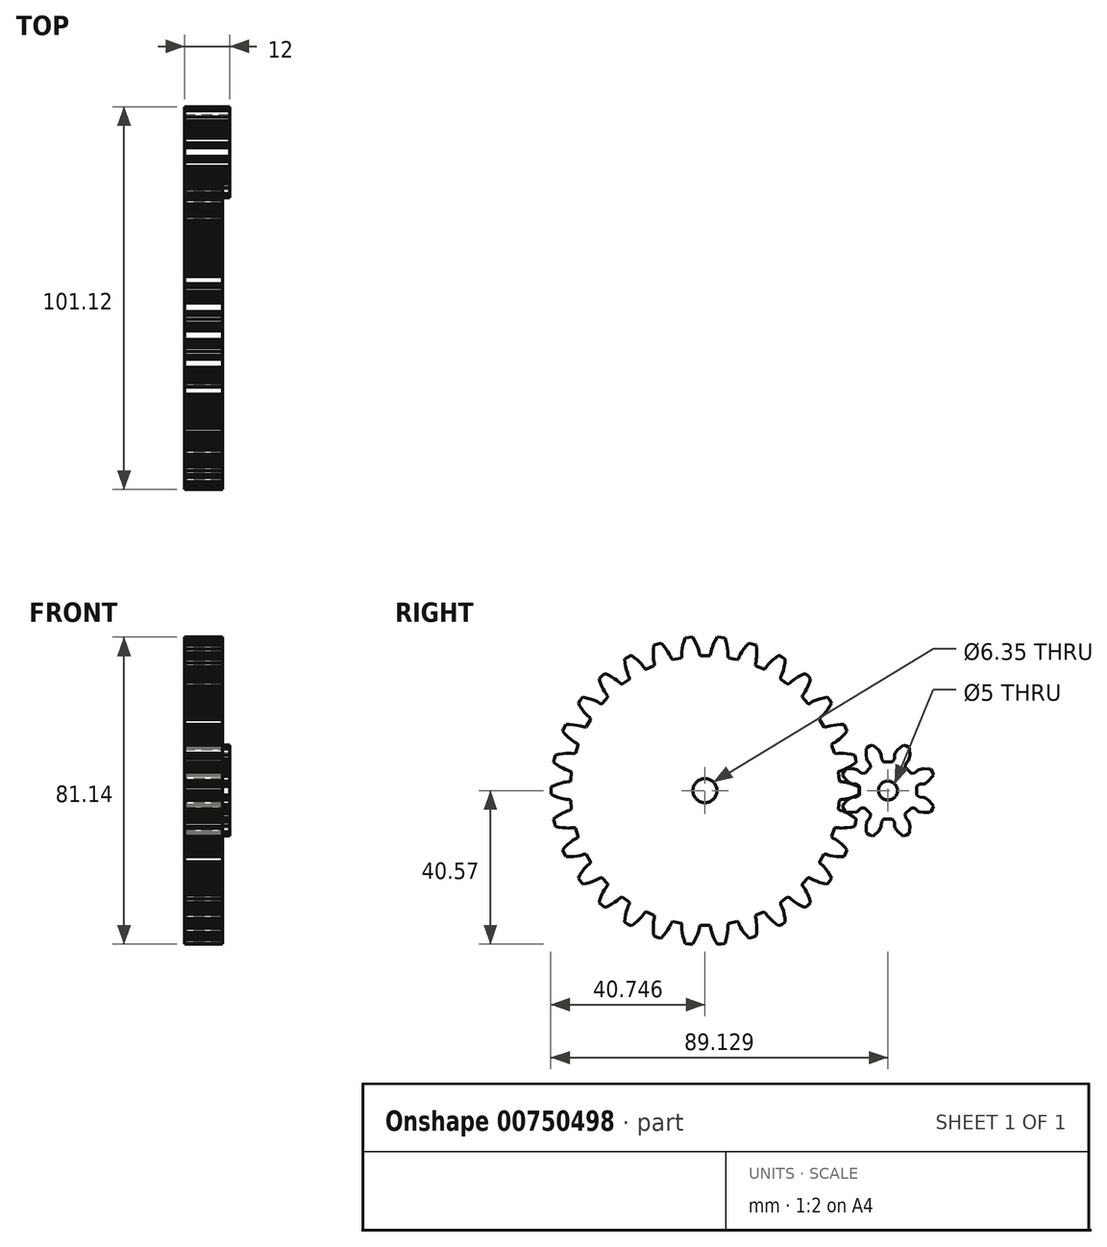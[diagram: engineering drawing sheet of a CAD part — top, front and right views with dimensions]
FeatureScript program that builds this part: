
annotation { "Feature Type Name" : "Feature", "Feature Type Description" : "" }
export const myFeature = defineFeature(function(context is Context, id is Id, definition is map)
    precondition{}
    {
        {
            var Q0;
            Q0=qCreatedBy(makeId("Right.planeOp"),FACE);
            var sketch = newSketch(context, id + "F0", { "sketchPlane" : qUnion([Q0])});
            skLineSegment(sketch, "E0", {"start": v(29.78, -9.42) * mm, "end": v(30.04, -8.47) * mm});
            skLineSegment(sketch, "E1", {"start": v(30.04, -8.47) * mm, "end": v(30.2, -7.5) * mm});
            skLineSegment(sketch, "E2", {"start": v(30.2, -7.5) * mm, "end": v(29.43, -6.92) * mm});
            skLineSegment(sketch, "E3", {"start": v(29.43, -6.92) * mm, "end": v(28.52, -6.34) * mm});
            skLineSegment(sketch, "E4", {"start": v(28.52, -6.34) * mm, "end": v(27.72, -5.9) * mm});
            skLineSegment(sketch, "E5", {"start": v(27.72, -5.9) * mm, "end": v(27.06, -5.6) * mm});
            skLineSegment(sketch, "E6", {"start": v(27.06, -5.6) * mm, "end": v(26.55, -5.4) * mm});
            skLineSegment(sketch, "E7", {"start": v(26.55, -5.4) * mm, "end": v(26, -5.23) * mm});
            skLineSegment(sketch, "E8", {"start": v(26, -5.23) * mm, "end": v(25.63, -5.05) * mm});
            skLineSegment(sketch, "E9", {"start": v(25.63, -5.05) * mm, "end": v(25.47, -4.85) * mm});
            skLineSegment(sketch, "E10", {"start": v(25.47, -4.85) * mm, "end": v(25.71, -2.59) * mm});
            skLineSegment(sketch, "E11", {"start": v(25.71, -2.59) * mm, "end": v(25.9, -2.43) * mm});
            skLineSegment(sketch, "E12", {"start": v(25.9, -2.43) * mm, "end": v(26.3, -2.33) * mm});
            skLineSegment(sketch, "E13", {"start": v(26.3, -2.33) * mm, "end": v(26.87, -2.28) * mm});
            skLineSegment(sketch, "E14", {"start": v(26.87, -2.28) * mm, "end": v(27.42, -2.2) * mm});
            skLineSegment(sketch, "E15", {"start": v(27.42, -2.2) * mm, "end": v(28.13, -2.04) * mm});
            skLineSegment(sketch, "E16", {"start": v(28.13, -2.04) * mm, "end": v(29, -1.77) * mm});
            skLineSegment(sketch, "E17", {"start": v(29, -1.77) * mm, "end": v(30, -1.39) * mm});
            skLineSegment(sketch, "E18", {"start": v(30, -1.39) * mm, "end": v(30.88, -0.98) * mm});
            skLineSegment(sketch, "E19", {"start": v(30.88, -0.98) * mm, "end": v(30.93, 0) * mm});
            skLineSegment(sketch, "E20", {"start": v(30.93, 0) * mm, "end": v(30.88, 0.98) * mm});
            skLineSegment(sketch, "E21", {"start": v(30.88, 0.98) * mm, "end": v(30, 1.39) * mm});
            skLineSegment(sketch, "E22", {"start": v(30, 1.39) * mm, "end": v(29, 1.77) * mm});
            skLineSegment(sketch, "E23", {"start": v(29, 1.77) * mm, "end": v(28.13, 2.04) * mm});
            skLineSegment(sketch, "E24", {"start": v(28.13, 2.04) * mm, "end": v(27.42, 2.2) * mm});
            skLineSegment(sketch, "E25", {"start": v(27.42, 2.2) * mm, "end": v(26.87, 2.28) * mm});
            skLineSegment(sketch, "E26", {"start": v(26.87, 2.28) * mm, "end": v(26.3, 2.33) * mm});
            skLineSegment(sketch, "E27", {"start": v(26.3, 2.33) * mm, "end": v(25.9, 2.43) * mm});
            skLineSegment(sketch, "E28", {"start": v(25.9, 2.43) * mm, "end": v(25.71, 2.59) * mm});
            skLineSegment(sketch, "E29", {"start": v(25.71, 2.59) * mm, "end": v(25.47, 4.85) * mm});
            skLineSegment(sketch, "E30", {"start": v(25.47, 4.85) * mm, "end": v(25.63, 5.05) * mm});
            skLineSegment(sketch, "E31", {"start": v(25.63, 5.05) * mm, "end": v(26, 5.23) * mm});
            skLineSegment(sketch, "E32", {"start": v(26, 5.23) * mm, "end": v(26.55, 5.4) * mm});
            skLineSegment(sketch, "E33", {"start": v(26.55, 5.4) * mm, "end": v(27.06, 5.6) * mm});
            skLineSegment(sketch, "E34", {"start": v(27.06, 5.6) * mm, "end": v(27.72, 5.9) * mm});
            skLineSegment(sketch, "E35", {"start": v(27.72, 5.9) * mm, "end": v(28.52, 6.34) * mm});
            skLineSegment(sketch, "E36", {"start": v(28.52, 6.34) * mm, "end": v(29.43, 6.92) * mm});
            skLineSegment(sketch, "E37", {"start": v(29.43, 6.92) * mm, "end": v(30.2, 7.5) * mm});
            skLineSegment(sketch, "E38", {"start": v(30.2, 7.5) * mm, "end": v(30.04, 8.47) * mm});
            skLineSegment(sketch, "E39", {"start": v(30.04, 8.47) * mm, "end": v(29.78, 9.42) * mm});
            skLineSegment(sketch, "E40", {"start": v(29.78, 9.42) * mm, "end": v(28.85, 9.64) * mm});
            skLineSegment(sketch, "E41", {"start": v(28.85, 9.64) * mm, "end": v(27.78, 9.8) * mm});
            skLineSegment(sketch, "E42", {"start": v(27.78, 9.8) * mm, "end": v(26.88, 9.88) * mm});
            skLineSegment(sketch, "E43", {"start": v(26.88, 9.88) * mm, "end": v(26.15, 9.9) * mm});
            skLineSegment(sketch, "E44", {"start": v(26.15, 9.9) * mm, "end": v(25.6, 9.86) * mm});
            skLineSegment(sketch, "E45", {"start": v(25.6, 9.86) * mm, "end": v(25.02, 9.79) * mm});
            skLineSegment(sketch, "E46", {"start": v(25.02, 9.79) * mm, "end": v(24.62, 9.8) * mm});
            skLineSegment(sketch, "E47", {"start": v(24.62, 9.8) * mm, "end": v(24.4, 9.92) * mm});
            skLineSegment(sketch, "E48", {"start": v(24.4, 9.92) * mm, "end": v(23.7, 12.08) * mm});
            skLineSegment(sketch, "E49", {"start": v(23.7, 12.08) * mm, "end": v(23.8, 12.3) * mm});
            skLineSegment(sketch, "E50", {"start": v(23.8, 12.3) * mm, "end": v(24.12, 12.56) * mm});
            skLineSegment(sketch, "E51", {"start": v(24.12, 12.56) * mm, "end": v(24.63, 12.84) * mm});
            skLineSegment(sketch, "E52", {"start": v(24.63, 12.84) * mm, "end": v(25.1, 13.14) * mm});
            skLineSegment(sketch, "E53", {"start": v(25.1, 13.14) * mm, "end": v(25.68, 13.57) * mm});
            skLineSegment(sketch, "E54", {"start": v(25.68, 13.57) * mm, "end": v(26.36, 14.17) * mm});
            skLineSegment(sketch, "E55", {"start": v(26.36, 14.17) * mm, "end": v(27.13, 14.93) * mm});
            skLineSegment(sketch, "E56", {"start": v(27.13, 14.93) * mm, "end": v(27.76, 15.65) * mm});
            skLineSegment(sketch, "E57", {"start": v(27.76, 15.65) * mm, "end": v(27.4, 16.57) * mm});
            skLineSegment(sketch, "E58", {"start": v(27.4, 16.57) * mm, "end": v(26.96, 17.45) * mm});
            skLineSegment(sketch, "E59", {"start": v(26.96, 17.45) * mm, "end": v(26, 17.46) * mm});
            skLineSegment(sketch, "E60", {"start": v(26, 17.46) * mm, "end": v(24.92, 17.4) * mm});
            skLineSegment(sketch, "E61", {"start": v(24.92, 17.4) * mm, "end": v(24.02, 17.3) * mm});
            skLineSegment(sketch, "E62", {"start": v(24.02, 17.3) * mm, "end": v(23.3, 17.15) * mm});
            skLineSegment(sketch, "E63", {"start": v(23.3, 17.15) * mm, "end": v(22.77, 17) * mm});
            skLineSegment(sketch, "E64", {"start": v(22.77, 17) * mm, "end": v(22.22, 16.82) * mm});
            skLineSegment(sketch, "E65", {"start": v(22.22, 16.82) * mm, "end": v(21.83, 16.75) * mm});
            skLineSegment(sketch, "E66", {"start": v(21.83, 16.75) * mm, "end": v(21.59, 16.81) * mm});
            skLineSegment(sketch, "E67", {"start": v(21.59, 16.81) * mm, "end": v(20.45, 18.79) * mm});
            skLineSegment(sketch, "E68", {"start": v(20.45, 18.79) * mm, "end": v(20.52, 19.03) * mm});
            skLineSegment(sketch, "E69", {"start": v(20.52, 19.03) * mm, "end": v(20.77, 19.34) * mm});
            skLineSegment(sketch, "E70", {"start": v(20.77, 19.34) * mm, "end": v(21.2, 19.72) * mm});
            skLineSegment(sketch, "E71", {"start": v(21.2, 19.72) * mm, "end": v(21.6, 20.1) * mm});
            skLineSegment(sketch, "E72", {"start": v(21.6, 20.1) * mm, "end": v(22.08, 20.66) * mm});
            skLineSegment(sketch, "E73", {"start": v(22.08, 20.66) * mm, "end": v(22.63, 21.38) * mm});
            skLineSegment(sketch, "E74", {"start": v(22.63, 21.38) * mm, "end": v(23.22, 22.28) * mm});
            skLineSegment(sketch, "E75", {"start": v(23.22, 22.28) * mm, "end": v(23.68, 23.12) * mm});
            skLineSegment(sketch, "E76", {"start": v(23.68, 23.12) * mm, "end": v(23.15, 23.95) * mm});
            skLineSegment(sketch, "E77", {"start": v(23.15, 23.95) * mm, "end": v(22.53, 24.71) * mm});
            skLineSegment(sketch, "E78", {"start": v(22.53, 24.71) * mm, "end": v(21.59, 24.53) * mm});
            skLineSegment(sketch, "E79", {"start": v(21.59, 24.53) * mm, "end": v(20.54, 24.25) * mm});
            skLineSegment(sketch, "E80", {"start": v(20.54, 24.25) * mm, "end": v(19.69, 23.95) * mm});
            skLineSegment(sketch, "E81", {"start": v(19.69, 23.95) * mm, "end": v(19.02, 23.66) * mm});
            skLineSegment(sketch, "E82", {"start": v(19.02, 23.66) * mm, "end": v(18.52, 23.41) * mm});
            skLineSegment(sketch, "E83", {"start": v(18.52, 23.41) * mm, "end": v(18.03, 23.11) * mm});
            skLineSegment(sketch, "E84", {"start": v(18.03, 23.11) * mm, "end": v(17.65, 22.97) * mm});
            skLineSegment(sketch, "E85", {"start": v(17.65, 22.97) * mm, "end": v(17.4, 22.98) * mm});
            skLineSegment(sketch, "E86", {"start": v(17.4, 22.98) * mm, "end": v(15.88, 24.67) * mm});
            skLineSegment(sketch, "E87", {"start": v(15.88, 24.67) * mm, "end": v(15.9, 24.92) * mm});
            skLineSegment(sketch, "E88", {"start": v(15.9, 24.92) * mm, "end": v(16.08, 25.27) * mm});
            skLineSegment(sketch, "E89", {"start": v(16.08, 25.27) * mm, "end": v(16.43, 25.74) * mm});
            skLineSegment(sketch, "E90", {"start": v(16.43, 25.74) * mm, "end": v(16.73, 26.2) * mm});
            skLineSegment(sketch, "E91", {"start": v(16.73, 26.2) * mm, "end": v(17.09, 26.84) * mm});
            skLineSegment(sketch, "E92", {"start": v(17.09, 26.84) * mm, "end": v(17.47, 27.66) * mm});
            skLineSegment(sketch, "E93", {"start": v(17.47, 27.66) * mm, "end": v(17.86, 28.67) * mm});
            skLineSegment(sketch, "E94", {"start": v(17.86, 28.67) * mm, "end": v(18.14, 29.58) * mm});
            skLineSegment(sketch, "E95", {"start": v(18.14, 29.58) * mm, "end": v(17.45, 30.28) * mm});
            skLineSegment(sketch, "E96", {"start": v(17.45, 30.28) * mm, "end": v(16.68, 30.9) * mm});
            skLineSegment(sketch, "E97", {"start": v(16.68, 30.9) * mm, "end": v(15.8, 30.52) * mm});
            skLineSegment(sketch, "E98", {"start": v(15.8, 30.52) * mm, "end": v(14.84, 30.03) * mm});
            skLineSegment(sketch, "E99", {"start": v(14.84, 30.03) * mm, "end": v(14.06, 29.56) * mm});
            skLineSegment(sketch, "E100", {"start": v(14.06, 29.56) * mm, "end": v(13.47, 29.14) * mm});
            skLineSegment(sketch, "E101", {"start": v(13.47, 29.14) * mm, "end": v(13.04, 28.8) * mm});
            skLineSegment(sketch, "E102", {"start": v(13.04, 28.8) * mm, "end": v(12.61, 28.4) * mm});
            skLineSegment(sketch, "E103", {"start": v(12.61, 28.4) * mm, "end": v(12.28, 28.17) * mm});
            skLineSegment(sketch, "E104", {"start": v(12.28, 28.17) * mm, "end": v(12.03, 28.13) * mm});
            skLineSegment(sketch, "E105", {"start": v(12.03, 28.13) * mm, "end": v(10.2, 29.47) * mm});
            skLineSegment(sketch, "E106", {"start": v(10.2, 29.47) * mm, "end": v(10.15, 29.72) * mm});
            skLineSegment(sketch, "E107", {"start": v(10.15, 29.72) * mm, "end": v(10.26, 30.1) * mm});
            skLineSegment(sketch, "E108", {"start": v(10.26, 30.1) * mm, "end": v(10.5, 30.63) * mm});
            skLineSegment(sketch, "E109", {"start": v(10.5, 30.63) * mm, "end": v(10.7, 31.15) * mm});
            skLineSegment(sketch, "E110", {"start": v(10.7, 31.15) * mm, "end": v(10.92, 31.84) * mm});
            skLineSegment(sketch, "E111", {"start": v(10.92, 31.84) * mm, "end": v(11.13, 32.73) * mm});
            skLineSegment(sketch, "E112", {"start": v(11.13, 32.73) * mm, "end": v(11.3, 33.8) * mm});
            skLineSegment(sketch, "E113", {"start": v(11.3, 33.8) * mm, "end": v(11.38, 34.75) * mm});
            skLineSegment(sketch, "E114", {"start": v(11.38, 34.75) * mm, "end": v(10.56, 35.29) * mm});
            skLineSegment(sketch, "E115", {"start": v(10.56, 35.29) * mm, "end": v(9.68, 35.73) * mm});
            skLineSegment(sketch, "E116", {"start": v(9.68, 35.73) * mm, "end": v(8.9, 35.18) * mm});
            skLineSegment(sketch, "E117", {"start": v(8.9, 35.18) * mm, "end": v(8.06, 34.5) * mm});
            skLineSegment(sketch, "E118", {"start": v(8.06, 34.5) * mm, "end": v(7.4, 33.88) * mm});
            skLineSegment(sketch, "E119", {"start": v(7.4, 33.88) * mm, "end": v(6.9, 33.34) * mm});
            skLineSegment(sketch, "E120", {"start": v(6.9, 33.34) * mm, "end": v(6.55, 32.91) * mm});
            skLineSegment(sketch, "E121", {"start": v(6.55, 32.91) * mm, "end": v(6.22, 32.44) * mm});
            skLineSegment(sketch, "E122", {"start": v(6.22, 32.44) * mm, "end": v(5.94, 32.15) * mm});
            skLineSegment(sketch, "E123", {"start": v(5.94, 32.15) * mm, "end": v(5.7, 32.06) * mm});
            skLineSegment(sketch, "E124", {"start": v(5.7, 32.06) * mm, "end": v(3.63, 32.99) * mm});
            skLineSegment(sketch, "E125", {"start": v(3.63, 32.99) * mm, "end": v(3.54, 33.22) * mm});
            skLineSegment(sketch, "E126", {"start": v(3.54, 33.22) * mm, "end": v(3.56, 33.62) * mm});
            skLineSegment(sketch, "E127", {"start": v(3.56, 33.62) * mm, "end": v(3.7, 34.19) * mm});
            skLineSegment(sketch, "E128", {"start": v(3.7, 34.19) * mm, "end": v(3.78, 34.73) * mm});
            skLineSegment(sketch, "E129", {"start": v(3.78, 34.73) * mm, "end": v(3.85, 35.46) * mm});
            skLineSegment(sketch, "E130", {"start": v(3.85, 35.46) * mm, "end": v(3.86, 36.36) * mm});
            skLineSegment(sketch, "E131", {"start": v(3.86, 36.36) * mm, "end": v(3.81, 37.44) * mm});
            skLineSegment(sketch, "E132", {"start": v(3.81, 37.44) * mm, "end": v(3.7, 38.4) * mm});
            skLineSegment(sketch, "E133", {"start": v(3.7, 38.4) * mm, "end": v(2.78, 38.75) * mm});
            skLineSegment(sketch, "E134", {"start": v(2.78, 38.75) * mm, "end": v(1.82, 39) * mm});
            skLineSegment(sketch, "E135", {"start": v(1.82, 39) * mm, "end": v(1.17, 38.3) * mm});
            skLineSegment(sketch, "E136", {"start": v(1.17, 38.3) * mm, "end": v(0.5, 37.46) * mm});
            skLineSegment(sketch, "E137", {"start": v(0.5, 37.46) * mm, "end": v(-0.02, 36.72) * mm});
            skLineSegment(sketch, "E138", {"start": v(-0.02, 36.72) * mm, "end": v(-0.4, 36.1) * mm});
            skLineSegment(sketch, "E139", {"start": v(-0.4, 36.1) * mm, "end": v(-0.65, 35.6) * mm});
            skLineSegment(sketch, "E140", {"start": v(-0.65, 35.6) * mm, "end": v(-0.87, 35.06) * mm});
            skLineSegment(sketch, "E141", {"start": v(-0.87, 35.06) * mm, "end": v(-1.1, 34.72) * mm});
            skLineSegment(sketch, "E142", {"start": v(-1.1, 34.72) * mm, "end": v(-1.3, 34.59) * mm});
            skLineSegment(sketch, "E143", {"start": v(-1.3, 34.59) * mm, "end": v(-3.53, 35.06) * mm});
            skLineSegment(sketch, "E144", {"start": v(-3.53, 35.06) * mm, "end": v(-3.66, 35.27) * mm});
            skLineSegment(sketch, "E145", {"start": v(-3.66, 35.27) * mm, "end": v(-3.72, 35.67) * mm});
            skLineSegment(sketch, "E146", {"start": v(-3.72, 35.67) * mm, "end": v(-3.7, 36.25) * mm});
            skLineSegment(sketch, "E147", {"start": v(-3.7, 36.25) * mm, "end": v(-3.74, 36.8) * mm});
            skLineSegment(sketch, "E148", {"start": v(-3.74, 36.8) * mm, "end": v(-3.82, 37.52) * mm});
            skLineSegment(sketch, "E149", {"start": v(-3.82, 37.52) * mm, "end": v(-4, 38.41) * mm});
            skLineSegment(sketch, "E150", {"start": v(-4, 38.41) * mm, "end": v(-4.27, 39.46) * mm});
            skLineSegment(sketch, "E151", {"start": v(-4.27, 39.46) * mm, "end": v(-4.58, 40.37) * mm});
            skLineSegment(sketch, "E152", {"start": v(-4.58, 40.37) * mm, "end": v(-5.56, 40.52) * mm});
            skLineSegment(sketch, "E153", {"start": v(-5.56, 40.52) * mm, "end": v(-6.54, 40.57) * mm});
            skLineSegment(sketch, "E154", {"start": v(-6.54, 40.57) * mm, "end": v(-7.03, 39.75) * mm});
            skLineSegment(sketch, "E155", {"start": v(-7.03, 39.75) * mm, "end": v(-7.52, 38.78) * mm});
            skLineSegment(sketch, "E156", {"start": v(-7.52, 38.78) * mm, "end": v(-7.87, 37.95) * mm});
            skLineSegment(sketch, "E157", {"start": v(-7.87, 37.95) * mm, "end": v(-8.1, 37.26) * mm});
            skLineSegment(sketch, "E158", {"start": v(-8.1, 37.26) * mm, "end": v(-8.25, 36.72) * mm});
            skLineSegment(sketch, "E159", {"start": v(-8.25, 36.72) * mm, "end": v(-8.36, 36.15) * mm});
            skLineSegment(sketch, "E160", {"start": v(-8.36, 36.15) * mm, "end": v(-8.5, 35.78) * mm});
            skLineSegment(sketch, "E161", {"start": v(-8.5, 35.78) * mm, "end": v(-8.68, 35.6) * mm});
            skLineSegment(sketch, "E162", {"start": v(-8.68, 35.6) * mm, "end": v(-10.95, 35.6) * mm});
            skLineSegment(sketch, "E163", {"start": v(-10.95, 35.6) * mm, "end": v(-11.13, 35.78) * mm});
            skLineSegment(sketch, "E164", {"start": v(-11.13, 35.78) * mm, "end": v(-11.27, 36.15) * mm});
            skLineSegment(sketch, "E165", {"start": v(-11.27, 36.15) * mm, "end": v(-11.38, 36.72) * mm});
            skLineSegment(sketch, "E166", {"start": v(-11.38, 36.72) * mm, "end": v(-11.52, 37.26) * mm});
            skLineSegment(sketch, "E167", {"start": v(-11.52, 37.26) * mm, "end": v(-11.76, 37.95) * mm});
            skLineSegment(sketch, "E168", {"start": v(-11.76, 37.95) * mm, "end": v(-12.1, 38.78) * mm});
            skLineSegment(sketch, "E169", {"start": v(-12.1, 38.78) * mm, "end": v(-12.6, 39.75) * mm});
            skLineSegment(sketch, "E170", {"start": v(-12.6, 39.75) * mm, "end": v(-13.09, 40.57) * mm});
            skLineSegment(sketch, "E171", {"start": v(-13.09, 40.57) * mm, "end": v(-14.07, 40.52) * mm});
            skLineSegment(sketch, "E172", {"start": v(-14.07, 40.52) * mm, "end": v(-15.05, 40.37) * mm});
            skLineSegment(sketch, "E173", {"start": v(-15.05, 40.37) * mm, "end": v(-15.36, 39.46) * mm});
            skLineSegment(sketch, "E174", {"start": v(-15.36, 39.46) * mm, "end": v(-15.63, 38.41) * mm});
            skLineSegment(sketch, "E175", {"start": v(-15.63, 38.41) * mm, "end": v(-15.8, 37.52) * mm});
            skLineSegment(sketch, "E176", {"start": v(-15.8, 37.52) * mm, "end": v(-15.9, 36.8) * mm});
            skLineSegment(sketch, "E177", {"start": v(-15.9, 36.8) * mm, "end": v(-15.92, 36.25) * mm});
            skLineSegment(sketch, "E178", {"start": v(-15.92, 36.25) * mm, "end": v(-15.9, 35.67) * mm});
            skLineSegment(sketch, "E179", {"start": v(-15.9, 35.67) * mm, "end": v(-15.97, 35.27) * mm});
            skLineSegment(sketch, "E180", {"start": v(-15.97, 35.27) * mm, "end": v(-16.1, 35.06) * mm});
            skLineSegment(sketch, "E181", {"start": v(-16.1, 35.06) * mm, "end": v(-18.33, 34.59) * mm});
            skLineSegment(sketch, "E182", {"start": v(-18.33, 34.59) * mm, "end": v(-18.54, 34.72) * mm});
            skLineSegment(sketch, "E183", {"start": v(-18.54, 34.72) * mm, "end": v(-18.75, 35.06) * mm});
            skLineSegment(sketch, "E184", {"start": v(-18.75, 35.06) * mm, "end": v(-18.98, 35.6) * mm});
            skLineSegment(sketch, "E185", {"start": v(-18.98, 35.6) * mm, "end": v(-19.23, 36.1) * mm});
            skLineSegment(sketch, "E186", {"start": v(-19.23, 36.1) * mm, "end": v(-19.6, 36.72) * mm});
            skLineSegment(sketch, "E187", {"start": v(-19.6, 36.72) * mm, "end": v(-20.12, 37.46) * mm});
            skLineSegment(sketch, "E188", {"start": v(-20.12, 37.46) * mm, "end": v(-20.8, 38.3) * mm});
            skLineSegment(sketch, "E189", {"start": v(-20.8, 38.3) * mm, "end": v(-21.45, 39) * mm});
            skLineSegment(sketch, "E190", {"start": v(-21.45, 39) * mm, "end": v(-22.4, 38.75) * mm});
            skLineSegment(sketch, "E191", {"start": v(-22.4, 38.75) * mm, "end": v(-23.32, 38.4) * mm});
            skLineSegment(sketch, "E192", {"start": v(-23.32, 38.4) * mm, "end": v(-23.44, 37.44) * mm});
            skLineSegment(sketch, "E193", {"start": v(-23.44, 37.44) * mm, "end": v(-23.5, 36.36) * mm});
            skLineSegment(sketch, "E194", {"start": v(-23.5, 36.36) * mm, "end": v(-23.48, 35.46) * mm});
            skLineSegment(sketch, "E195", {"start": v(-23.48, 35.46) * mm, "end": v(-23.41, 34.73) * mm});
            skLineSegment(sketch, "E196", {"start": v(-23.41, 34.73) * mm, "end": v(-23.32, 34.19) * mm});
            skLineSegment(sketch, "E197", {"start": v(-23.32, 34.19) * mm, "end": v(-23.2, 33.62) * mm});
            skLineSegment(sketch, "E198", {"start": v(-23.2, 33.62) * mm, "end": v(-23.17, 33.22) * mm});
            skLineSegment(sketch, "E199", {"start": v(-23.17, 33.22) * mm, "end": v(-23.25, 32.99) * mm});
            skLineSegment(sketch, "E200", {"start": v(-23.25, 32.99) * mm, "end": v(-25.33, 32.06) * mm});
            skLineSegment(sketch, "E201", {"start": v(-25.33, 32.06) * mm, "end": v(-25.57, 32.15) * mm});
            skLineSegment(sketch, "E202", {"start": v(-25.57, 32.15) * mm, "end": v(-25.85, 32.44) * mm});
            skLineSegment(sketch, "E203", {"start": v(-25.85, 32.44) * mm, "end": v(-26.18, 32.91) * mm});
            skLineSegment(sketch, "E204", {"start": v(-26.18, 32.91) * mm, "end": v(-26.53, 33.34) * mm});
            skLineSegment(sketch, "E205", {"start": v(-26.53, 33.34) * mm, "end": v(-27.02, 33.88) * mm});
            skLineSegment(sketch, "E206", {"start": v(-27.02, 33.88) * mm, "end": v(-27.68, 34.5) * mm});
            skLineSegment(sketch, "E207", {"start": v(-27.68, 34.5) * mm, "end": v(-28.52, 35.18) * mm});
            skLineSegment(sketch, "E208", {"start": v(-28.52, 35.18) * mm, "end": v(-29.3, 35.73) * mm});
            skLineSegment(sketch, "E209", {"start": v(-29.3, 35.73) * mm, "end": v(-30.19, 35.29) * mm});
            skLineSegment(sketch, "E210", {"start": v(-30.19, 35.29) * mm, "end": v(-31.01, 34.75) * mm});
            skLineSegment(sketch, "E211", {"start": v(-31.01, 34.75) * mm, "end": v(-30.93, 33.8) * mm});
            skLineSegment(sketch, "E212", {"start": v(-30.93, 33.8) * mm, "end": v(-30.76, 32.73) * mm});
            skLineSegment(sketch, "E213", {"start": v(-30.76, 32.73) * mm, "end": v(-30.55, 31.84) * mm});
            skLineSegment(sketch, "E214", {"start": v(-30.55, 31.84) * mm, "end": v(-30.33, 31.15) * mm});
            skLineSegment(sketch, "E215", {"start": v(-30.33, 31.15) * mm, "end": v(-30.14, 30.63) * mm});
            skLineSegment(sketch, "E216", {"start": v(-30.14, 30.63) * mm, "end": v(-29.89, 30.1) * mm});
            skLineSegment(sketch, "E217", {"start": v(-29.89, 30.1) * mm, "end": v(-29.78, 29.72) * mm});
            skLineSegment(sketch, "E218", {"start": v(-29.78, 29.72) * mm, "end": v(-29.82, 29.47) * mm});
            skLineSegment(sketch, "E219", {"start": v(-29.82, 29.47) * mm, "end": v(-31.66, 28.13) * mm});
            skLineSegment(sketch, "E220", {"start": v(-31.66, 28.13) * mm, "end": v(-31.9, 28.17) * mm});
            skLineSegment(sketch, "E221", {"start": v(-31.9, 28.17) * mm, "end": v(-32.24, 28.4) * mm});
            skLineSegment(sketch, "E222", {"start": v(-32.24, 28.4) * mm, "end": v(-32.67, 28.8) * mm});
            skLineSegment(sketch, "E223", {"start": v(-32.67, 28.8) * mm, "end": v(-33.1, 29.14) * mm});
            skLineSegment(sketch, "E224", {"start": v(-33.1, 29.14) * mm, "end": v(-33.7, 29.56) * mm});
            skLineSegment(sketch, "E225", {"start": v(-33.7, 29.56) * mm, "end": v(-34.47, 30.03) * mm});
            skLineSegment(sketch, "E226", {"start": v(-34.47, 30.03) * mm, "end": v(-35.43, 30.52) * mm});
            skLineSegment(sketch, "E227", {"start": v(-35.43, 30.52) * mm, "end": v(-36.31, 30.9) * mm});
            skLineSegment(sketch, "E228", {"start": v(-36.31, 30.9) * mm, "end": v(-37.08, 30.28) * mm});
            skLineSegment(sketch, "E229", {"start": v(-37.08, 30.28) * mm, "end": v(-37.77, 29.58) * mm});
            skLineSegment(sketch, "E230", {"start": v(-37.77, 29.58) * mm, "end": v(-37.5, 28.67) * mm});
            skLineSegment(sketch, "E231", {"start": v(-37.5, 28.67) * mm, "end": v(-37.1, 27.66) * mm});
            skLineSegment(sketch, "E232", {"start": v(-37.1, 27.66) * mm, "end": v(-36.72, 26.84) * mm});
            skLineSegment(sketch, "E233", {"start": v(-36.72, 26.84) * mm, "end": v(-36.36, 26.2) * mm});
            skLineSegment(sketch, "E234", {"start": v(-36.36, 26.2) * mm, "end": v(-36.06, 25.74) * mm});
            skLineSegment(sketch, "E235", {"start": v(-36.06, 25.74) * mm, "end": v(-35.7, 25.27) * mm});
            skLineSegment(sketch, "E236", {"start": v(-35.7, 25.27) * mm, "end": v(-35.53, 24.92) * mm});
            skLineSegment(sketch, "E237", {"start": v(-35.53, 24.92) * mm, "end": v(-35.5, 24.67) * mm});
            skLineSegment(sketch, "E238", {"start": v(-35.5, 24.67) * mm, "end": v(-37.03, 22.98) * mm});
            skLineSegment(sketch, "E239", {"start": v(-37.03, 22.98) * mm, "end": v(-37.28, 22.97) * mm});
            skLineSegment(sketch, "E240", {"start": v(-37.28, 22.97) * mm, "end": v(-37.66, 23.11) * mm});
            skLineSegment(sketch, "E241", {"start": v(-37.66, 23.11) * mm, "end": v(-38.15, 23.41) * mm});
            skLineSegment(sketch, "E242", {"start": v(-38.15, 23.41) * mm, "end": v(-38.64, 23.66) * mm});
            skLineSegment(sketch, "E243", {"start": v(-38.64, 23.66) * mm, "end": v(-39.32, 23.95) * mm});
            skLineSegment(sketch, "E244", {"start": v(-39.32, 23.95) * mm, "end": v(-40.17, 24.25) * mm});
            skLineSegment(sketch, "E245", {"start": v(-40.17, 24.25) * mm, "end": v(-41.22, 24.53) * mm});
            skLineSegment(sketch, "E246", {"start": v(-41.22, 24.53) * mm, "end": v(-42.16, 24.71) * mm});
            skLineSegment(sketch, "E247", {"start": v(-42.16, 24.71) * mm, "end": v(-42.78, 23.95) * mm});
            skLineSegment(sketch, "E248", {"start": v(-42.78, 23.95) * mm, "end": v(-43.31, 23.12) * mm});
            skLineSegment(sketch, "E249", {"start": v(-43.31, 23.12) * mm, "end": v(-42.85, 22.28) * mm});
            skLineSegment(sketch, "E250", {"start": v(-42.85, 22.28) * mm, "end": v(-42.26, 21.38) * mm});
            skLineSegment(sketch, "E251", {"start": v(-42.26, 21.38) * mm, "end": v(-41.7, 20.66) * mm});
            skLineSegment(sketch, "E252", {"start": v(-41.7, 20.66) * mm, "end": v(-41.23, 20.1) * mm});
            skLineSegment(sketch, "E253", {"start": v(-41.23, 20.1) * mm, "end": v(-40.84, 19.72) * mm});
            skLineSegment(sketch, "E254", {"start": v(-40.84, 19.72) * mm, "end": v(-40.4, 19.34) * mm});
            skLineSegment(sketch, "E255", {"start": v(-40.4, 19.34) * mm, "end": v(-40.14, 19.03) * mm});
            skLineSegment(sketch, "E256", {"start": v(-40.14, 19.03) * mm, "end": v(-40.08, 18.79) * mm});
            skLineSegment(sketch, "E257", {"start": v(-40.08, 18.79) * mm, "end": v(-41.21, 16.81) * mm});
            skLineSegment(sketch, "E258", {"start": v(-41.21, 16.81) * mm, "end": v(-41.46, 16.75) * mm});
            skLineSegment(sketch, "E259", {"start": v(-41.46, 16.75) * mm, "end": v(-41.85, 16.82) * mm});
            skLineSegment(sketch, "E260", {"start": v(-41.85, 16.82) * mm, "end": v(-42.4, 17) * mm});
            skLineSegment(sketch, "E261", {"start": v(-42.4, 17) * mm, "end": v(-42.93, 17.15) * mm});
            skLineSegment(sketch, "E262", {"start": v(-42.93, 17.15) * mm, "end": v(-43.65, 17.3) * mm});
            skLineSegment(sketch, "E263", {"start": v(-43.65, 17.3) * mm, "end": v(-44.55, 17.4) * mm});
            skLineSegment(sketch, "E264", {"start": v(-44.55, 17.4) * mm, "end": v(-45.63, 17.46) * mm});
            skLineSegment(sketch, "E265", {"start": v(-45.63, 17.46) * mm, "end": v(-46.59, 17.45) * mm});
            skLineSegment(sketch, "E266", {"start": v(-46.59, 17.45) * mm, "end": v(-47.04, 16.57) * mm});
            skLineSegment(sketch, "E267", {"start": v(-47.04, 16.57) * mm, "end": v(-47.39, 15.65) * mm});
            skLineSegment(sketch, "E268", {"start": v(-47.39, 15.65) * mm, "end": v(-46.76, 14.93) * mm});
            skLineSegment(sketch, "E269", {"start": v(-46.76, 14.93) * mm, "end": v(-46, 14.17) * mm});
            skLineSegment(sketch, "E270", {"start": v(-46, 14.17) * mm, "end": v(-45.3, 13.57) * mm});
            skLineSegment(sketch, "E271", {"start": v(-45.3, 13.57) * mm, "end": v(-44.72, 13.14) * mm});
            skLineSegment(sketch, "E272", {"start": v(-44.72, 13.14) * mm, "end": v(-44.26, 12.84) * mm});
            skLineSegment(sketch, "E273", {"start": v(-44.26, 12.84) * mm, "end": v(-43.75, 12.56) * mm});
            skLineSegment(sketch, "E274", {"start": v(-43.75, 12.56) * mm, "end": v(-43.44, 12.3) * mm});
            skLineSegment(sketch, "E275", {"start": v(-43.44, 12.3) * mm, "end": v(-43.32, 12.08) * mm});
            skLineSegment(sketch, "E276", {"start": v(-43.32, 12.08) * mm, "end": v(-44.02, 9.92) * mm});
            skLineSegment(sketch, "E277", {"start": v(-44.02, 9.92) * mm, "end": v(-44.25, 9.8) * mm});
            skLineSegment(sketch, "E278", {"start": v(-44.25, 9.8) * mm, "end": v(-44.65, 9.79) * mm});
            skLineSegment(sketch, "E279", {"start": v(-44.65, 9.79) * mm, "end": v(-45.22, 9.86) * mm});
            skLineSegment(sketch, "E280", {"start": v(-45.22, 9.86) * mm, "end": v(-45.78, 9.9) * mm});
            skLineSegment(sketch, "E281", {"start": v(-45.78, 9.9) * mm, "end": v(-46.5, 9.88) * mm});
            skLineSegment(sketch, "E282", {"start": v(-46.5, 9.88) * mm, "end": v(-47.4, 9.8) * mm});
            skLineSegment(sketch, "E283", {"start": v(-47.4, 9.8) * mm, "end": v(-48.48, 9.64) * mm});
            skLineSegment(sketch, "E284", {"start": v(-48.48, 9.64) * mm, "end": v(-49.41, 9.42) * mm});
            skLineSegment(sketch, "E285", {"start": v(-49.41, 9.42) * mm, "end": v(-49.67, 8.47) * mm});
            skLineSegment(sketch, "E286", {"start": v(-49.67, 8.47) * mm, "end": v(-49.82, 7.5) * mm});
            skLineSegment(sketch, "E287", {"start": v(-49.82, 7.5) * mm, "end": v(-49.05, 6.92) * mm});
            skLineSegment(sketch, "E288", {"start": v(-49.05, 6.92) * mm, "end": v(-48.15, 6.34) * mm});
            skLineSegment(sketch, "E289", {"start": v(-48.15, 6.34) * mm, "end": v(-47.35, 5.9) * mm});
            skLineSegment(sketch, "E290", {"start": v(-47.35, 5.9) * mm, "end": v(-46.7, 5.6) * mm});
            skLineSegment(sketch, "E291", {"start": v(-46.7, 5.6) * mm, "end": v(-46.17, 5.4) * mm});
            skLineSegment(sketch, "E292", {"start": v(-46.17, 5.4) * mm, "end": v(-45.62, 5.23) * mm});
            skLineSegment(sketch, "E293", {"start": v(-45.62, 5.23) * mm, "end": v(-45.26, 5.05) * mm});
            skLineSegment(sketch, "E294", {"start": v(-45.26, 5.05) * mm, "end": v(-45.1, 4.85) * mm});
            skLineSegment(sketch, "E295", {"start": v(-45.1, 4.85) * mm, "end": v(-45.34, 2.59) * mm});
            skLineSegment(sketch, "E296", {"start": v(-45.34, 2.59) * mm, "end": v(-45.54, 2.43) * mm});
            skLineSegment(sketch, "E297", {"start": v(-45.54, 2.43) * mm, "end": v(-45.92, 2.33) * mm});
            skLineSegment(sketch, "E298", {"start": v(-45.92, 2.33) * mm, "end": v(-46.5, 2.28) * mm});
            skLineSegment(sketch, "E299", {"start": v(-46.5, 2.28) * mm, "end": v(-47.05, 2.2) * mm});
            skLineSegment(sketch, "E300", {"start": v(-47.05, 2.2) * mm, "end": v(-47.76, 2.04) * mm});
            skLineSegment(sketch, "E301", {"start": v(-47.76, 2.04) * mm, "end": v(-48.63, 1.77) * mm});
            skLineSegment(sketch, "E302", {"start": v(-48.63, 1.77) * mm, "end": v(-49.64, 1.39) * mm});
            skLineSegment(sketch, "E303", {"start": v(-49.64, 1.39) * mm, "end": v(-50.5, 0.98) * mm});
            skLineSegment(sketch, "E304", {"start": v(-50.5, 0.98) * mm, "end": v(-50.56, 0) * mm});
            skLineSegment(sketch, "E305", {"start": v(-50.56, 0) * mm, "end": v(-50.5, -0.98) * mm});
            skLineSegment(sketch, "E306", {"start": v(-50.5, -0.98) * mm, "end": v(-49.64, -1.39) * mm});
            skLineSegment(sketch, "E307", {"start": v(-49.64, -1.39) * mm, "end": v(-48.63, -1.77) * mm});
            skLineSegment(sketch, "E308", {"start": v(-48.63, -1.77) * mm, "end": v(-47.76, -2.04) * mm});
            skLineSegment(sketch, "E309", {"start": v(-47.76, -2.04) * mm, "end": v(-47.05, -2.2) * mm});
            skLineSegment(sketch, "E310", {"start": v(-47.05, -2.2) * mm, "end": v(-46.5, -2.28) * mm});
            skLineSegment(sketch, "E311", {"start": v(-46.5, -2.28) * mm, "end": v(-45.92, -2.33) * mm});
            skLineSegment(sketch, "E312", {"start": v(-45.92, -2.33) * mm, "end": v(-45.54, -2.43) * mm});
            skLineSegment(sketch, "E313", {"start": v(-45.54, -2.43) * mm, "end": v(-45.34, -2.59) * mm});
            skLineSegment(sketch, "E314", {"start": v(-45.34, -2.59) * mm, "end": v(-45.1, -4.85) * mm});
            skLineSegment(sketch, "E315", {"start": v(-45.1, -4.85) * mm, "end": v(-45.26, -5.05) * mm});
            skLineSegment(sketch, "E316", {"start": v(-45.26, -5.05) * mm, "end": v(-45.62, -5.23) * mm});
            skLineSegment(sketch, "E317", {"start": v(-45.62, -5.23) * mm, "end": v(-46.17, -5.4) * mm});
            skLineSegment(sketch, "E318", {"start": v(-46.17, -5.4) * mm, "end": v(-46.7, -5.6) * mm});
            skLineSegment(sketch, "E319", {"start": v(-46.7, -5.6) * mm, "end": v(-47.35, -5.9) * mm});
            skLineSegment(sketch, "E320", {"start": v(-47.35, -5.9) * mm, "end": v(-48.15, -6.34) * mm});
            skLineSegment(sketch, "E321", {"start": v(-48.15, -6.34) * mm, "end": v(-49.05, -6.92) * mm});
            skLineSegment(sketch, "E322", {"start": v(-49.05, -6.92) * mm, "end": v(-49.82, -7.5) * mm});
            skLineSegment(sketch, "E323", {"start": v(-49.82, -7.5) * mm, "end": v(-49.67, -8.47) * mm});
            skLineSegment(sketch, "E324", {"start": v(-49.67, -8.47) * mm, "end": v(-49.41, -9.42) * mm});
            skLineSegment(sketch, "E325", {"start": v(-49.41, -9.42) * mm, "end": v(-48.48, -9.64) * mm});
            skLineSegment(sketch, "E326", {"start": v(-48.48, -9.64) * mm, "end": v(-47.4, -9.8) * mm});
            skLineSegment(sketch, "E327", {"start": v(-47.4, -9.8) * mm, "end": v(-46.5, -9.88) * mm});
            skLineSegment(sketch, "E328", {"start": v(-46.5, -9.88) * mm, "end": v(-45.78, -9.9) * mm});
            skLineSegment(sketch, "E329", {"start": v(-45.78, -9.9) * mm, "end": v(-45.22, -9.86) * mm});
            skLineSegment(sketch, "E330", {"start": v(-45.22, -9.86) * mm, "end": v(-44.65, -9.79) * mm});
            skLineSegment(sketch, "E331", {"start": v(-44.65, -9.79) * mm, "end": v(-44.25, -9.8) * mm});
            skLineSegment(sketch, "E332", {"start": v(-44.25, -9.8) * mm, "end": v(-44.02, -9.92) * mm});
            skLineSegment(sketch, "E333", {"start": v(-44.02, -9.92) * mm, "end": v(-43.32, -12.08) * mm});
            skLineSegment(sketch, "E334", {"start": v(-43.32, -12.08) * mm, "end": v(-43.44, -12.3) * mm});
            skLineSegment(sketch, "E335", {"start": v(-43.44, -12.3) * mm, "end": v(-43.75, -12.56) * mm});
            skLineSegment(sketch, "E336", {"start": v(-43.75, -12.56) * mm, "end": v(-44.26, -12.84) * mm});
            skLineSegment(sketch, "E337", {"start": v(-44.26, -12.84) * mm, "end": v(-44.72, -13.14) * mm});
            skLineSegment(sketch, "E338", {"start": v(-44.72, -13.14) * mm, "end": v(-45.3, -13.57) * mm});
            skLineSegment(sketch, "E339", {"start": v(-45.3, -13.57) * mm, "end": v(-46, -14.17) * mm});
            skLineSegment(sketch, "E340", {"start": v(-46, -14.17) * mm, "end": v(-46.76, -14.93) * mm});
            skLineSegment(sketch, "E341", {"start": v(-46.76, -14.93) * mm, "end": v(-47.39, -15.65) * mm});
            skLineSegment(sketch, "E342", {"start": v(-47.39, -15.65) * mm, "end": v(-47.04, -16.57) * mm});
            skLineSegment(sketch, "E343", {"start": v(-47.04, -16.57) * mm, "end": v(-46.59, -17.45) * mm});
            skLineSegment(sketch, "E344", {"start": v(-46.59, -17.45) * mm, "end": v(-45.63, -17.46) * mm});
            skLineSegment(sketch, "E345", {"start": v(-45.63, -17.46) * mm, "end": v(-44.55, -17.4) * mm});
            skLineSegment(sketch, "E346", {"start": v(-44.55, -17.4) * mm, "end": v(-43.65, -17.3) * mm});
            skLineSegment(sketch, "E347", {"start": v(-43.65, -17.3) * mm, "end": v(-42.93, -17.15) * mm});
            skLineSegment(sketch, "E348", {"start": v(-42.93, -17.15) * mm, "end": v(-42.4, -17) * mm});
            skLineSegment(sketch, "E349", {"start": v(-42.4, -17) * mm, "end": v(-41.85, -16.82) * mm});
            skLineSegment(sketch, "E350", {"start": v(-41.85, -16.82) * mm, "end": v(-41.46, -16.75) * mm});
            skLineSegment(sketch, "E351", {"start": v(-41.46, -16.75) * mm, "end": v(-41.21, -16.81) * mm});
            skLineSegment(sketch, "E352", {"start": v(-41.21, -16.81) * mm, "end": v(-40.08, -18.79) * mm});
            skLineSegment(sketch, "E353", {"start": v(-40.08, -18.79) * mm, "end": v(-40.14, -19.03) * mm});
            skLineSegment(sketch, "E354", {"start": v(-40.14, -19.03) * mm, "end": v(-40.4, -19.34) * mm});
            skLineSegment(sketch, "E355", {"start": v(-40.4, -19.34) * mm, "end": v(-40.84, -19.72) * mm});
            skLineSegment(sketch, "E356", {"start": v(-40.84, -19.72) * mm, "end": v(-41.23, -20.1) * mm});
            skLineSegment(sketch, "E357", {"start": v(-41.23, -20.1) * mm, "end": v(-41.7, -20.66) * mm});
            skLineSegment(sketch, "E358", {"start": v(-41.7, -20.66) * mm, "end": v(-42.26, -21.38) * mm});
            skLineSegment(sketch, "E359", {"start": v(-42.26, -21.38) * mm, "end": v(-42.85, -22.28) * mm});
            skLineSegment(sketch, "E360", {"start": v(-42.85, -22.28) * mm, "end": v(-43.31, -23.12) * mm});
            skLineSegment(sketch, "E361", {"start": v(-43.31, -23.12) * mm, "end": v(-42.78, -23.95) * mm});
            skLineSegment(sketch, "E362", {"start": v(-42.78, -23.95) * mm, "end": v(-42.16, -24.71) * mm});
            skLineSegment(sketch, "E363", {"start": v(-42.16, -24.71) * mm, "end": v(-41.22, -24.53) * mm});
            skLineSegment(sketch, "E364", {"start": v(-41.22, -24.53) * mm, "end": v(-40.17, -24.25) * mm});
            skLineSegment(sketch, "E365", {"start": v(-40.17, -24.25) * mm, "end": v(-39.32, -23.95) * mm});
            skLineSegment(sketch, "E366", {"start": v(-39.32, -23.95) * mm, "end": v(-38.64, -23.66) * mm});
            skLineSegment(sketch, "E367", {"start": v(-38.64, -23.66) * mm, "end": v(-38.15, -23.41) * mm});
            skLineSegment(sketch, "E368", {"start": v(-38.15, -23.41) * mm, "end": v(-37.66, -23.11) * mm});
            skLineSegment(sketch, "E369", {"start": v(-37.66, -23.11) * mm, "end": v(-37.28, -22.97) * mm});
            skLineSegment(sketch, "E370", {"start": v(-37.28, -22.97) * mm, "end": v(-37.03, -22.98) * mm});
            skLineSegment(sketch, "E371", {"start": v(-37.03, -22.98) * mm, "end": v(-35.5, -24.67) * mm});
            skLineSegment(sketch, "E372", {"start": v(-35.5, -24.67) * mm, "end": v(-35.53, -24.92) * mm});
            skLineSegment(sketch, "E373", {"start": v(-35.53, -24.92) * mm, "end": v(-35.7, -25.27) * mm});
            skLineSegment(sketch, "E374", {"start": v(-35.7, -25.27) * mm, "end": v(-36.06, -25.74) * mm});
            skLineSegment(sketch, "E375", {"start": v(-36.06, -25.74) * mm, "end": v(-36.36, -26.2) * mm});
            skLineSegment(sketch, "E376", {"start": v(-36.36, -26.2) * mm, "end": v(-36.72, -26.84) * mm});
            skLineSegment(sketch, "E377", {"start": v(-36.72, -26.84) * mm, "end": v(-37.1, -27.66) * mm});
            skLineSegment(sketch, "E378", {"start": v(-37.1, -27.66) * mm, "end": v(-37.5, -28.67) * mm});
            skLineSegment(sketch, "E379", {"start": v(-37.5, -28.67) * mm, "end": v(-37.77, -29.58) * mm});
            skLineSegment(sketch, "E380", {"start": v(-37.77, -29.58) * mm, "end": v(-37.08, -30.28) * mm});
            skLineSegment(sketch, "E381", {"start": v(-37.08, -30.28) * mm, "end": v(-36.31, -30.9) * mm});
            skLineSegment(sketch, "E382", {"start": v(-36.31, -30.9) * mm, "end": v(-35.43, -30.52) * mm});
            skLineSegment(sketch, "E383", {"start": v(-35.43, -30.52) * mm, "end": v(-34.47, -30.03) * mm});
            skLineSegment(sketch, "E384", {"start": v(-34.47, -30.03) * mm, "end": v(-33.7, -29.56) * mm});
            skLineSegment(sketch, "E385", {"start": v(-33.7, -29.56) * mm, "end": v(-33.1, -29.14) * mm});
            skLineSegment(sketch, "E386", {"start": v(-33.1, -29.14) * mm, "end": v(-32.67, -28.8) * mm});
            skLineSegment(sketch, "E387", {"start": v(-32.67, -28.8) * mm, "end": v(-32.24, -28.4) * mm});
            skLineSegment(sketch, "E388", {"start": v(-32.24, -28.4) * mm, "end": v(-31.9, -28.17) * mm});
            skLineSegment(sketch, "E389", {"start": v(-31.9, -28.17) * mm, "end": v(-31.66, -28.13) * mm});
            skLineSegment(sketch, "E390", {"start": v(-31.66, -28.13) * mm, "end": v(-29.82, -29.47) * mm});
            skLineSegment(sketch, "E391", {"start": v(-29.82, -29.47) * mm, "end": v(-29.78, -29.72) * mm});
            skLineSegment(sketch, "E392", {"start": v(-29.78, -29.72) * mm, "end": v(-29.89, -30.1) * mm});
            skLineSegment(sketch, "E393", {"start": v(-29.89, -30.1) * mm, "end": v(-30.14, -30.63) * mm});
            skLineSegment(sketch, "E394", {"start": v(-30.14, -30.63) * mm, "end": v(-30.33, -31.15) * mm});
            skLineSegment(sketch, "E395", {"start": v(-30.33, -31.15) * mm, "end": v(-30.55, -31.84) * mm});
            skLineSegment(sketch, "E396", {"start": v(-30.55, -31.84) * mm, "end": v(-30.76, -32.73) * mm});
            skLineSegment(sketch, "E397", {"start": v(-30.76, -32.73) * mm, "end": v(-30.93, -33.8) * mm});
            skLineSegment(sketch, "E398", {"start": v(-30.93, -33.8) * mm, "end": v(-31.01, -34.75) * mm});
            skLineSegment(sketch, "E399", {"start": v(-31.01, -34.75) * mm, "end": v(-30.19, -35.29) * mm});
            skLineSegment(sketch, "E400", {"start": v(-30.19, -35.29) * mm, "end": v(-29.3, -35.73) * mm});
            skLineSegment(sketch, "E401", {"start": v(-29.3, -35.73) * mm, "end": v(-28.52, -35.18) * mm});
            skLineSegment(sketch, "E402", {"start": v(-28.52, -35.18) * mm, "end": v(-27.68, -34.5) * mm});
            skLineSegment(sketch, "E403", {"start": v(-27.68, -34.5) * mm, "end": v(-27.02, -33.88) * mm});
            skLineSegment(sketch, "E404", {"start": v(-27.02, -33.88) * mm, "end": v(-26.53, -33.34) * mm});
            skLineSegment(sketch, "E405", {"start": v(-26.53, -33.34) * mm, "end": v(-26.18, -32.91) * mm});
            skLineSegment(sketch, "E406", {"start": v(-26.18, -32.91) * mm, "end": v(-25.85, -32.44) * mm});
            skLineSegment(sketch, "E407", {"start": v(-25.85, -32.44) * mm, "end": v(-25.57, -32.15) * mm});
            skLineSegment(sketch, "E408", {"start": v(-25.57, -32.15) * mm, "end": v(-25.33, -32.06) * mm});
            skLineSegment(sketch, "E409", {"start": v(-25.33, -32.06) * mm, "end": v(-23.25, -32.99) * mm});
            skLineSegment(sketch, "E410", {"start": v(-23.25, -32.99) * mm, "end": v(-23.17, -33.22) * mm});
            skLineSegment(sketch, "E411", {"start": v(-23.17, -33.22) * mm, "end": v(-23.2, -33.62) * mm});
            skLineSegment(sketch, "E412", {"start": v(-23.2, -33.62) * mm, "end": v(-23.32, -34.19) * mm});
            skLineSegment(sketch, "E413", {"start": v(-23.32, -34.19) * mm, "end": v(-23.41, -34.73) * mm});
            skLineSegment(sketch, "E414", {"start": v(-23.41, -34.73) * mm, "end": v(-23.48, -35.46) * mm});
            skLineSegment(sketch, "E415", {"start": v(-23.48, -35.46) * mm, "end": v(-23.5, -36.36) * mm});
            skLineSegment(sketch, "E416", {"start": v(-23.5, -36.36) * mm, "end": v(-23.44, -37.44) * mm});
            skLineSegment(sketch, "E417", {"start": v(-23.44, -37.44) * mm, "end": v(-23.32, -38.4) * mm});
            skLineSegment(sketch, "E418", {"start": v(-23.32, -38.4) * mm, "end": v(-22.4, -38.75) * mm});
            skLineSegment(sketch, "E419", {"start": v(-22.4, -38.75) * mm, "end": v(-21.45, -39) * mm});
            skLineSegment(sketch, "E420", {"start": v(-21.45, -39) * mm, "end": v(-20.8, -38.3) * mm});
            skLineSegment(sketch, "E421", {"start": v(-20.8, -38.3) * mm, "end": v(-20.12, -37.46) * mm});
            skLineSegment(sketch, "E422", {"start": v(-20.12, -37.46) * mm, "end": v(-19.6, -36.72) * mm});
            skLineSegment(sketch, "E423", {"start": v(-19.6, -36.72) * mm, "end": v(-19.23, -36.1) * mm});
            skLineSegment(sketch, "E424", {"start": v(-19.23, -36.1) * mm, "end": v(-18.98, -35.6) * mm});
            skLineSegment(sketch, "E425", {"start": v(-18.98, -35.6) * mm, "end": v(-18.75, -35.06) * mm});
            skLineSegment(sketch, "E426", {"start": v(-18.75, -35.06) * mm, "end": v(-18.54, -34.72) * mm});
            skLineSegment(sketch, "E427", {"start": v(-18.54, -34.72) * mm, "end": v(-18.33, -34.59) * mm});
            skLineSegment(sketch, "E428", {"start": v(-18.33, -34.59) * mm, "end": v(-16.1, -35.06) * mm});
            skLineSegment(sketch, "E429", {"start": v(-16.1, -35.06) * mm, "end": v(-15.97, -35.27) * mm});
            skLineSegment(sketch, "E430", {"start": v(-15.97, -35.27) * mm, "end": v(-15.9, -35.67) * mm});
            skLineSegment(sketch, "E431", {"start": v(-15.9, -35.67) * mm, "end": v(-15.92, -36.25) * mm});
            skLineSegment(sketch, "E432", {"start": v(-15.92, -36.25) * mm, "end": v(-15.9, -36.8) * mm});
            skLineSegment(sketch, "E433", {"start": v(-15.9, -36.8) * mm, "end": v(-15.8, -37.52) * mm});
            skLineSegment(sketch, "E434", {"start": v(-15.8, -37.52) * mm, "end": v(-15.63, -38.41) * mm});
            skLineSegment(sketch, "E435", {"start": v(-15.63, -38.41) * mm, "end": v(-15.36, -39.46) * mm});
            skLineSegment(sketch, "E436", {"start": v(-15.36, -39.46) * mm, "end": v(-15.05, -40.37) * mm});
            skLineSegment(sketch, "E437", {"start": v(-15.05, -40.37) * mm, "end": v(-14.07, -40.52) * mm});
            skLineSegment(sketch, "E438", {"start": v(-14.07, -40.52) * mm, "end": v(-13.09, -40.57) * mm});
            skLineSegment(sketch, "E439", {"start": v(-13.09, -40.57) * mm, "end": v(-12.6, -39.75) * mm});
            skLineSegment(sketch, "E440", {"start": v(-12.6, -39.75) * mm, "end": v(-12.1, -38.78) * mm});
            skLineSegment(sketch, "E441", {"start": v(-12.1, -38.78) * mm, "end": v(-11.76, -37.95) * mm});
            skLineSegment(sketch, "E442", {"start": v(-11.76, -37.95) * mm, "end": v(-11.52, -37.26) * mm});
            skLineSegment(sketch, "E443", {"start": v(-11.52, -37.26) * mm, "end": v(-11.38, -36.72) * mm});
            skLineSegment(sketch, "E444", {"start": v(-11.38, -36.72) * mm, "end": v(-11.27, -36.15) * mm});
            skLineSegment(sketch, "E445", {"start": v(-11.27, -36.15) * mm, "end": v(-11.13, -35.78) * mm});
            skLineSegment(sketch, "E446", {"start": v(-11.13, -35.78) * mm, "end": v(-10.95, -35.6) * mm});
            skLineSegment(sketch, "E447", {"start": v(-10.95, -35.6) * mm, "end": v(-8.68, -35.6) * mm});
            skLineSegment(sketch, "E448", {"start": v(-8.68, -35.6) * mm, "end": v(-8.5, -35.78) * mm});
            skLineSegment(sketch, "E449", {"start": v(-8.5, -35.78) * mm, "end": v(-8.36, -36.15) * mm});
            skLineSegment(sketch, "E450", {"start": v(-8.36, -36.15) * mm, "end": v(-8.25, -36.72) * mm});
            skLineSegment(sketch, "E451", {"start": v(-8.25, -36.72) * mm, "end": v(-8.1, -37.26) * mm});
            skLineSegment(sketch, "E452", {"start": v(-8.1, -37.26) * mm, "end": v(-7.87, -37.95) * mm});
            skLineSegment(sketch, "E453", {"start": v(-7.87, -37.95) * mm, "end": v(-7.52, -38.78) * mm});
            skLineSegment(sketch, "E454", {"start": v(-7.52, -38.78) * mm, "end": v(-7.03, -39.75) * mm});
            skLineSegment(sketch, "E455", {"start": v(-7.03, -39.75) * mm, "end": v(-6.54, -40.57) * mm});
            skLineSegment(sketch, "E456", {"start": v(-6.54, -40.57) * mm, "end": v(-5.56, -40.52) * mm});
            skLineSegment(sketch, "E457", {"start": v(-5.56, -40.52) * mm, "end": v(-4.58, -40.37) * mm});
            skLineSegment(sketch, "E458", {"start": v(-4.58, -40.37) * mm, "end": v(-4.27, -39.46) * mm});
            skLineSegment(sketch, "E459", {"start": v(-4.27, -39.46) * mm, "end": v(-4, -38.41) * mm});
            skLineSegment(sketch, "E460", {"start": v(-4, -38.41) * mm, "end": v(-3.82, -37.52) * mm});
            skLineSegment(sketch, "E461", {"start": v(-3.82, -37.52) * mm, "end": v(-3.74, -36.8) * mm});
            skLineSegment(sketch, "E462", {"start": v(-3.74, -36.8) * mm, "end": v(-3.7, -36.25) * mm});
            skLineSegment(sketch, "E463", {"start": v(-3.7, -36.25) * mm, "end": v(-3.72, -35.67) * mm});
            skLineSegment(sketch, "E464", {"start": v(-3.72, -35.67) * mm, "end": v(-3.66, -35.27) * mm});
            skLineSegment(sketch, "E465", {"start": v(-3.66, -35.27) * mm, "end": v(-3.53, -35.06) * mm});
            skLineSegment(sketch, "E466", {"start": v(-3.53, -35.06) * mm, "end": v(-1.3, -34.59) * mm});
            skLineSegment(sketch, "E467", {"start": v(-1.3, -34.59) * mm, "end": v(-1.1, -34.72) * mm});
            skLineSegment(sketch, "E468", {"start": v(-1.1, -34.72) * mm, "end": v(-0.87, -35.06) * mm});
            skLineSegment(sketch, "E469", {"start": v(-0.87, -35.06) * mm, "end": v(-0.65, -35.6) * mm});
            skLineSegment(sketch, "E470", {"start": v(-0.65, -35.6) * mm, "end": v(-0.4, -36.1) * mm});
            skLineSegment(sketch, "E471", {"start": v(-0.4, -36.1) * mm, "end": v(-0.02, -36.72) * mm});
            skLineSegment(sketch, "E472", {"start": v(-0.02, -36.72) * mm, "end": v(0.5, -37.46) * mm});
            skLineSegment(sketch, "E473", {"start": v(0.5, -37.46) * mm, "end": v(1.17, -38.3) * mm});
            skLineSegment(sketch, "E474", {"start": v(1.17, -38.3) * mm, "end": v(1.82, -39) * mm});
            skLineSegment(sketch, "E475", {"start": v(1.82, -39) * mm, "end": v(2.78, -38.75) * mm});
            skLineSegment(sketch, "E476", {"start": v(2.78, -38.75) * mm, "end": v(3.7, -38.4) * mm});
            skLineSegment(sketch, "E477", {"start": v(3.7, -38.4) * mm, "end": v(3.81, -37.44) * mm});
            skLineSegment(sketch, "E478", {"start": v(3.81, -37.44) * mm, "end": v(3.86, -36.36) * mm});
            skLineSegment(sketch, "E479", {"start": v(3.86, -36.36) * mm, "end": v(3.85, -35.46) * mm});
            skLineSegment(sketch, "E480", {"start": v(3.85, -35.46) * mm, "end": v(3.78, -34.73) * mm});
            skLineSegment(sketch, "E481", {"start": v(3.78, -34.73) * mm, "end": v(3.7, -34.19) * mm});
            skLineSegment(sketch, "E482", {"start": v(3.7, -34.19) * mm, "end": v(3.56, -33.62) * mm});
            skLineSegment(sketch, "E483", {"start": v(3.56, -33.62) * mm, "end": v(3.54, -33.22) * mm});
            skLineSegment(sketch, "E484", {"start": v(3.54, -33.22) * mm, "end": v(3.63, -32.99) * mm});
            skLineSegment(sketch, "E485", {"start": v(3.63, -32.99) * mm, "end": v(5.7, -32.06) * mm});
            skLineSegment(sketch, "E486", {"start": v(5.7, -32.06) * mm, "end": v(5.94, -32.15) * mm});
            skLineSegment(sketch, "E487", {"start": v(5.94, -32.15) * mm, "end": v(6.22, -32.44) * mm});
            skLineSegment(sketch, "E488", {"start": v(6.22, -32.44) * mm, "end": v(6.55, -32.91) * mm});
            skLineSegment(sketch, "E489", {"start": v(6.55, -32.91) * mm, "end": v(6.9, -33.34) * mm});
            skLineSegment(sketch, "E490", {"start": v(6.9, -33.34) * mm, "end": v(7.4, -33.88) * mm});
            skLineSegment(sketch, "E491", {"start": v(7.4, -33.88) * mm, "end": v(8.06, -34.5) * mm});
            skLineSegment(sketch, "E492", {"start": v(8.06, -34.5) * mm, "end": v(8.9, -35.18) * mm});
            skLineSegment(sketch, "E493", {"start": v(8.9, -35.18) * mm, "end": v(9.68, -35.73) * mm});
            skLineSegment(sketch, "E494", {"start": v(9.68, -35.73) * mm, "end": v(10.56, -35.29) * mm});
            skLineSegment(sketch, "E495", {"start": v(10.56, -35.29) * mm, "end": v(11.38, -34.75) * mm});
            skLineSegment(sketch, "E496", {"start": v(11.38, -34.75) * mm, "end": v(11.3, -33.8) * mm});
            skLineSegment(sketch, "E497", {"start": v(11.3, -33.8) * mm, "end": v(11.13, -32.73) * mm});
            skLineSegment(sketch, "E498", {"start": v(11.13, -32.73) * mm, "end": v(10.92, -31.84) * mm});
            skLineSegment(sketch, "E499", {"start": v(10.92, -31.84) * mm, "end": v(10.7, -31.15) * mm});
            skLineSegment(sketch, "E500", {"start": v(10.7, -31.15) * mm, "end": v(10.5, -30.63) * mm});
            skLineSegment(sketch, "E501", {"start": v(10.5, -30.63) * mm, "end": v(10.26, -30.1) * mm});
            skLineSegment(sketch, "E502", {"start": v(10.26, -30.1) * mm, "end": v(10.15, -29.72) * mm});
            skLineSegment(sketch, "E503", {"start": v(10.15, -29.72) * mm, "end": v(10.2, -29.47) * mm});
            skLineSegment(sketch, "E504", {"start": v(10.2, -29.47) * mm, "end": v(12.03, -28.13) * mm});
            skLineSegment(sketch, "E505", {"start": v(12.03, -28.13) * mm, "end": v(12.28, -28.17) * mm});
            skLineSegment(sketch, "E506", {"start": v(12.28, -28.17) * mm, "end": v(12.61, -28.4) * mm});
            skLineSegment(sketch, "E507", {"start": v(12.61, -28.4) * mm, "end": v(13.04, -28.8) * mm});
            skLineSegment(sketch, "E508", {"start": v(13.04, -28.8) * mm, "end": v(13.47, -29.14) * mm});
            skLineSegment(sketch, "E509", {"start": v(13.47, -29.14) * mm, "end": v(14.06, -29.56) * mm});
            skLineSegment(sketch, "E510", {"start": v(14.06, -29.56) * mm, "end": v(14.84, -30.03) * mm});
            skLineSegment(sketch, "E511", {"start": v(14.84, -30.03) * mm, "end": v(15.8, -30.52) * mm});
            skLineSegment(sketch, "E512", {"start": v(15.8, -30.52) * mm, "end": v(16.68, -30.9) * mm});
            skLineSegment(sketch, "E513", {"start": v(16.68, -30.9) * mm, "end": v(17.45, -30.28) * mm});
            skLineSegment(sketch, "E514", {"start": v(17.45, -30.28) * mm, "end": v(18.14, -29.58) * mm});
            skLineSegment(sketch, "E515", {"start": v(18.14, -29.58) * mm, "end": v(17.86, -28.67) * mm});
            skLineSegment(sketch, "E516", {"start": v(17.86, -28.67) * mm, "end": v(17.47, -27.66) * mm});
            skLineSegment(sketch, "E517", {"start": v(17.47, -27.66) * mm, "end": v(17.09, -26.84) * mm});
            skLineSegment(sketch, "E518", {"start": v(17.09, -26.84) * mm, "end": v(16.73, -26.2) * mm});
            skLineSegment(sketch, "E519", {"start": v(16.73, -26.2) * mm, "end": v(16.43, -25.74) * mm});
            skLineSegment(sketch, "E520", {"start": v(16.43, -25.74) * mm, "end": v(16.08, -25.27) * mm});
            skLineSegment(sketch, "E521", {"start": v(16.08, -25.27) * mm, "end": v(15.9, -24.92) * mm});
            skLineSegment(sketch, "E522", {"start": v(15.9, -24.92) * mm, "end": v(15.88, -24.67) * mm});
            skLineSegment(sketch, "E523", {"start": v(15.88, -24.67) * mm, "end": v(17.4, -22.98) * mm});
            skLineSegment(sketch, "E524", {"start": v(17.4, -22.98) * mm, "end": v(17.65, -22.97) * mm});
            skLineSegment(sketch, "E525", {"start": v(17.65, -22.97) * mm, "end": v(18.03, -23.11) * mm});
            skLineSegment(sketch, "E526", {"start": v(18.03, -23.11) * mm, "end": v(18.52, -23.41) * mm});
            skLineSegment(sketch, "E527", {"start": v(18.52, -23.41) * mm, "end": v(19.02, -23.66) * mm});
            skLineSegment(sketch, "E528", {"start": v(19.02, -23.66) * mm, "end": v(19.69, -23.95) * mm});
            skLineSegment(sketch, "E529", {"start": v(19.69, -23.95) * mm, "end": v(20.54, -24.25) * mm});
            skLineSegment(sketch, "E530", {"start": v(20.54, -24.25) * mm, "end": v(21.59, -24.53) * mm});
            skLineSegment(sketch, "E531", {"start": v(21.59, -24.53) * mm, "end": v(22.53, -24.71) * mm});
            skLineSegment(sketch, "E532", {"start": v(22.53, -24.71) * mm, "end": v(23.15, -23.95) * mm});
            skLineSegment(sketch, "E533", {"start": v(23.15, -23.95) * mm, "end": v(23.68, -23.12) * mm});
            skLineSegment(sketch, "E534", {"start": v(23.68, -23.12) * mm, "end": v(23.22, -22.28) * mm});
            skLineSegment(sketch, "E535", {"start": v(23.22, -22.28) * mm, "end": v(22.63, -21.38) * mm});
            skLineSegment(sketch, "E536", {"start": v(22.63, -21.38) * mm, "end": v(22.08, -20.66) * mm});
            skLineSegment(sketch, "E537", {"start": v(22.08, -20.66) * mm, "end": v(21.6, -20.1) * mm});
            skLineSegment(sketch, "E538", {"start": v(21.6, -20.1) * mm, "end": v(21.2, -19.72) * mm});
            skLineSegment(sketch, "E539", {"start": v(21.2, -19.72) * mm, "end": v(20.77, -19.34) * mm});
            skLineSegment(sketch, "E540", {"start": v(20.77, -19.34) * mm, "end": v(20.52, -19.03) * mm});
            skLineSegment(sketch, "E541", {"start": v(20.52, -19.03) * mm, "end": v(20.45, -18.79) * mm});
            skLineSegment(sketch, "E542", {"start": v(20.45, -18.79) * mm, "end": v(21.59, -16.81) * mm});
            skLineSegment(sketch, "E543", {"start": v(21.59, -16.81) * mm, "end": v(21.83, -16.75) * mm});
            skLineSegment(sketch, "E544", {"start": v(21.83, -16.75) * mm, "end": v(22.22, -16.82) * mm});
            skLineSegment(sketch, "E545", {"start": v(22.22, -16.82) * mm, "end": v(22.77, -17) * mm});
            skLineSegment(sketch, "E546", {"start": v(22.77, -17) * mm, "end": v(23.3, -17.15) * mm});
            skLineSegment(sketch, "E547", {"start": v(23.3, -17.15) * mm, "end": v(24.02, -17.3) * mm});
            skLineSegment(sketch, "E548", {"start": v(24.02, -17.3) * mm, "end": v(24.92, -17.4) * mm});
            skLineSegment(sketch, "E549", {"start": v(24.92, -17.4) * mm, "end": v(26, -17.46) * mm});
            skLineSegment(sketch, "E550", {"start": v(26, -17.46) * mm, "end": v(26.96, -17.45) * mm});
            skLineSegment(sketch, "E551", {"start": v(26.96, -17.45) * mm, "end": v(27.4, -16.57) * mm});
            skLineSegment(sketch, "E552", {"start": v(27.4, -16.57) * mm, "end": v(27.76, -15.65) * mm});
            skLineSegment(sketch, "E553", {"start": v(27.76, -15.65) * mm, "end": v(27.13, -14.93) * mm});
            skLineSegment(sketch, "E554", {"start": v(27.13, -14.93) * mm, "end": v(26.36, -14.17) * mm});
            skLineSegment(sketch, "E555", {"start": v(26.36, -14.17) * mm, "end": v(25.68, -13.57) * mm});
            skLineSegment(sketch, "E556", {"start": v(25.68, -13.57) * mm, "end": v(25.1, -13.14) * mm});
            skLineSegment(sketch, "E557", {"start": v(25.1, -13.14) * mm, "end": v(24.63, -12.84) * mm});
            skLineSegment(sketch, "E558", {"start": v(24.63, -12.84) * mm, "end": v(24.12, -12.56) * mm});
            skLineSegment(sketch, "E559", {"start": v(24.12, -12.56) * mm, "end": v(23.8, -12.3) * mm});
            skLineSegment(sketch, "E560", {"start": v(23.8, -12.3) * mm, "end": v(23.7, -12.08) * mm});
            skLineSegment(sketch, "E561", {"start": v(23.7, -12.08) * mm, "end": v(24.4, -9.92) * mm});
            skLineSegment(sketch, "E562", {"start": v(24.4, -9.92) * mm, "end": v(24.62, -9.8) * mm});
            skLineSegment(sketch, "E563", {"start": v(24.62, -9.8) * mm, "end": v(25.02, -9.79) * mm});
            skLineSegment(sketch, "E564", {"start": v(25.02, -9.79) * mm, "end": v(25.6, -9.86) * mm});
            skLineSegment(sketch, "E565", {"start": v(25.6, -9.86) * mm, "end": v(26.15, -9.9) * mm});
            skLineSegment(sketch, "E566", {"start": v(26.15, -9.9) * mm, "end": v(26.88, -9.88) * mm});
            skLineSegment(sketch, "E567", {"start": v(26.88, -9.88) * mm, "end": v(27.78, -9.8) * mm});
            skLineSegment(sketch, "E568", {"start": v(27.78, -9.8) * mm, "end": v(28.85, -9.64) * mm});
            skLineSegment(sketch, "E569", {"start": v(28.85, -9.64) * mm, "end": v(29.78, -9.42) * mm});
            skLineSegment(sketch, "E570", {"start": v(-9.4, -1.96) * mm, "end": v(-9.81, -2) * mm});
            skLineSegment(sketch, "E571", {"start": v(-9.81, -2) * mm, "end": v(-10.23, -1.96) * mm});
            skLineSegment(sketch, "E572", {"start": v(-10.23, -1.96) * mm, "end": v(-10.63, -1.83) * mm});
            skLineSegment(sketch, "E573", {"start": v(-10.63, -1.83) * mm, "end": v(-10.99, -1.62) * mm});
            skLineSegment(sketch, "E574", {"start": v(-10.99, -1.62) * mm, "end": v(-11.3, -1.34) * mm});
            skLineSegment(sketch, "E575", {"start": v(-11.3, -1.34) * mm, "end": v(-11.55, -1) * mm});
            skLineSegment(sketch, "E576", {"start": v(-11.55, -1) * mm, "end": v(-11.72, -0.62) * mm});
            skLineSegment(sketch, "E577", {"start": v(-11.72, -0.62) * mm, "end": v(-11.8, -0.2) * mm});
            skLineSegment(sketch, "E578", {"start": v(-11.8, -0.2) * mm, "end": v(-11.8, 0.2) * mm});
            skLineSegment(sketch, "E579", {"start": v(-11.8, 0.2) * mm, "end": v(-11.72, 0.62) * mm});
            skLineSegment(sketch, "E580", {"start": v(-11.72, 0.62) * mm, "end": v(-11.55, 1) * mm});
            skLineSegment(sketch, "E581", {"start": v(-11.55, 1) * mm, "end": v(-11.3, 1.34) * mm});
            skLineSegment(sketch, "E582", {"start": v(-11.3, 1.34) * mm, "end": v(-10.99, 1.62) * mm});
            skLineSegment(sketch, "E583", {"start": v(-10.99, 1.62) * mm, "end": v(-10.63, 1.83) * mm});
            skLineSegment(sketch, "E584", {"start": v(-10.63, 1.83) * mm, "end": v(-10.23, 1.96) * mm});
            skLineSegment(sketch, "E585", {"start": v(-10.23, 1.96) * mm, "end": v(-9.81, 2) * mm});
            skLineSegment(sketch, "E586", {"start": v(-9.81, 2) * mm, "end": v(-9.4, 1.96) * mm});
            skLineSegment(sketch, "E587", {"start": v(-9.4, 1.96) * mm, "end": v(-9, 1.83) * mm});
            skLineSegment(sketch, "E588", {"start": v(-9, 1.83) * mm, "end": v(-8.64, 1.62) * mm});
            skLineSegment(sketch, "E589", {"start": v(-8.64, 1.62) * mm, "end": v(-8.33, 1.34) * mm});
            skLineSegment(sketch, "E590", {"start": v(-8.33, 1.34) * mm, "end": v(-8.08, 1) * mm});
            skLineSegment(sketch, "E591", {"start": v(-8.08, 1) * mm, "end": v(-7.91, 0.62) * mm});
            skLineSegment(sketch, "E592", {"start": v(-7.91, 0.62) * mm, "end": v(-7.83, 0.2) * mm});
            skLineSegment(sketch, "E593", {"start": v(-7.83, 0.2) * mm, "end": v(-7.83, -0.2) * mm});
            skLineSegment(sketch, "E594", {"start": v(-7.83, -0.2) * mm, "end": v(-7.91, -0.62) * mm});
            skLineSegment(sketch, "E595", {"start": v(-7.91, -0.62) * mm, "end": v(-8.08, -1) * mm});
            skLineSegment(sketch, "E596", {"start": v(-8.08, -1) * mm, "end": v(-8.33, -1.34) * mm});
            skLineSegment(sketch, "E597", {"start": v(-8.33, -1.34) * mm, "end": v(-8.64, -1.62) * mm});
            skLineSegment(sketch, "E598", {"start": v(-8.64, -1.62) * mm, "end": v(-9, -1.83) * mm});
            skLineSegment(sketch, "E599", {"start": v(-9, -1.83) * mm, "end": v(-9.4, -1.96) * mm});
            skLineSegment(sketch, "E600", {"start": v(27.17, 5.56) * mm, "end": v(26.8, 4.87) * mm});
            skLineSegment(sketch, "E601", {"start": v(26.8, 4.87) * mm, "end": v(26.58, 4.13) * mm});
            skLineSegment(sketch, "E602", {"start": v(26.58, 4.13) * mm, "end": v(26.76, 3.76) * mm});
            skLineSegment(sketch, "E603", {"start": v(26.76, 3.76) * mm, "end": v(27.87, 2.48) * mm});
            skLineSegment(sketch, "E604", {"start": v(27.87, 2.48) * mm, "end": v(28.73, 1.9) * mm});
            skLineSegment(sketch, "E605", {"start": v(28.73, 1.9) * mm, "end": v(29.07, 1.8) * mm});
            skLineSegment(sketch, "E606", {"start": v(29.07, 1.8) * mm, "end": v(30.25, 1.71) * mm});
            skLineSegment(sketch, "E607", {"start": v(30.25, 1.71) * mm, "end": v(30.98, 1.14) * mm});
            skLineSegment(sketch, "E608", {"start": v(30.98, 1.14) * mm, "end": v(30.98, -1.14) * mm});
            skLineSegment(sketch, "E609", {"start": v(30.98, -1.14) * mm, "end": v(30.25, -1.71) * mm});
            skLineSegment(sketch, "E610", {"start": v(30.25, -1.71) * mm, "end": v(29.07, -1.8) * mm});
            skLineSegment(sketch, "E611", {"start": v(29.07, -1.8) * mm, "end": v(28.73, -1.9) * mm});
            skLineSegment(sketch, "E612", {"start": v(28.73, -1.9) * mm, "end": v(27.87, -2.48) * mm});
            skLineSegment(sketch, "E613", {"start": v(27.87, -2.48) * mm, "end": v(26.76, -3.76) * mm});
            skLineSegment(sketch, "E614", {"start": v(26.76, -3.76) * mm, "end": v(26.58, -4.13) * mm});
            skLineSegment(sketch, "E615", {"start": v(26.58, -4.13) * mm, "end": v(26.8, -4.87) * mm});
            skLineSegment(sketch, "E616", {"start": v(26.8, -4.87) * mm, "end": v(27.17, -5.56) * mm});
            skLineSegment(sketch, "E617", {"start": v(27.17, -5.56) * mm, "end": v(27.56, -5.7) * mm});
            skLineSegment(sketch, "E618", {"start": v(27.56, -5.7) * mm, "end": v(29.25, -5.8) * mm});
            skLineSegment(sketch, "E619", {"start": v(29.25, -5.8) * mm, "end": v(30.26, -5.6) * mm});
            skLineSegment(sketch, "E620", {"start": v(30.26, -5.6) * mm, "end": v(30.59, -5.45) * mm});
            skLineSegment(sketch, "E621", {"start": v(30.59, -5.45) * mm, "end": v(31.48, -4.67) * mm});
            skLineSegment(sketch, "E622", {"start": v(31.48, -4.67) * mm, "end": v(32.4, -4.56) * mm});
            skLineSegment(sketch, "E623", {"start": v(32.4, -4.56) * mm, "end": v(34, -6.17) * mm});
            skLineSegment(sketch, "E624", {"start": v(34, -6.17) * mm, "end": v(33.9, -7.1) * mm});
            skLineSegment(sketch, "E625", {"start": v(33.9, -7.1) * mm, "end": v(33.12, -7.98) * mm});
            skLineSegment(sketch, "E626", {"start": v(33.12, -7.98) * mm, "end": v(32.96, -8.3) * mm});
            skLineSegment(sketch, "E627", {"start": v(32.96, -8.3) * mm, "end": v(32.76, -9.32) * mm});
            skLineSegment(sketch, "E628", {"start": v(32.76, -9.32) * mm, "end": v(32.88, -11) * mm});
            skLineSegment(sketch, "E629", {"start": v(32.88, -11) * mm, "end": v(33, -11.4) * mm});
            skLineSegment(sketch, "E630", {"start": v(33, -11.4) * mm, "end": v(33.7, -11.76) * mm});
            skLineSegment(sketch, "E631", {"start": v(33.7, -11.76) * mm, "end": v(34.44, -11.99) * mm});
            skLineSegment(sketch, "E632", {"start": v(34.44, -11.99) * mm, "end": v(34.81, -11.8) * mm});
            skLineSegment(sketch, "E633", {"start": v(34.81, -11.8) * mm, "end": v(36.09, -10.7) * mm});
            skLineSegment(sketch, "E634", {"start": v(36.09, -10.7) * mm, "end": v(36.66, -9.84) * mm});
            skLineSegment(sketch, "E635", {"start": v(36.66, -9.84) * mm, "end": v(36.78, -9.5) * mm});
            skLineSegment(sketch, "E636", {"start": v(36.78, -9.5) * mm, "end": v(36.86, -8.32) * mm});
            skLineSegment(sketch, "E637", {"start": v(36.86, -8.32) * mm, "end": v(37.43, -7.59) * mm});
            skLineSegment(sketch, "E638", {"start": v(37.43, -7.59) * mm, "end": v(39.7, -7.59) * mm});
            skLineSegment(sketch, "E639", {"start": v(39.7, -7.59) * mm, "end": v(40.28, -8.32) * mm});
            skLineSegment(sketch, "E640", {"start": v(40.28, -8.32) * mm, "end": v(40.36, -9.5) * mm});
            skLineSegment(sketch, "E641", {"start": v(40.36, -9.5) * mm, "end": v(40.48, -9.84) * mm});
            skLineSegment(sketch, "E642", {"start": v(40.48, -9.84) * mm, "end": v(41.05, -10.7) * mm});
            skLineSegment(sketch, "E643", {"start": v(41.05, -10.7) * mm, "end": v(42.32, -11.8) * mm});
            skLineSegment(sketch, "E644", {"start": v(42.32, -11.8) * mm, "end": v(42.7, -11.99) * mm});
            skLineSegment(sketch, "E645", {"start": v(42.7, -11.99) * mm, "end": v(43.44, -11.76) * mm});
            skLineSegment(sketch, "E646", {"start": v(43.44, -11.76) * mm, "end": v(44.13, -11.4) * mm});
            skLineSegment(sketch, "E647", {"start": v(44.13, -11.4) * mm, "end": v(44.26, -11) * mm});
            skLineSegment(sketch, "E648", {"start": v(44.26, -11) * mm, "end": v(44.38, -9.32) * mm});
            skLineSegment(sketch, "E649", {"start": v(44.38, -9.32) * mm, "end": v(44.18, -8.3) * mm});
            skLineSegment(sketch, "E650", {"start": v(44.18, -8.3) * mm, "end": v(44.02, -7.98) * mm});
            skLineSegment(sketch, "E651", {"start": v(44.02, -7.98) * mm, "end": v(43.24, -7.1) * mm});
            skLineSegment(sketch, "E652", {"start": v(43.24, -7.1) * mm, "end": v(43.13, -6.17) * mm});
            skLineSegment(sketch, "E653", {"start": v(43.13, -6.17) * mm, "end": v(44.74, -4.56) * mm});
            skLineSegment(sketch, "E654", {"start": v(44.74, -4.56) * mm, "end": v(45.66, -4.67) * mm});
            skLineSegment(sketch, "E655", {"start": v(45.66, -4.67) * mm, "end": v(46.55, -5.45) * mm});
            skLineSegment(sketch, "E656", {"start": v(46.55, -5.45) * mm, "end": v(46.88, -5.6) * mm});
            skLineSegment(sketch, "E657", {"start": v(46.88, -5.6) * mm, "end": v(47.89, -5.8) * mm});
            skLineSegment(sketch, "E658", {"start": v(47.89, -5.8) * mm, "end": v(49.57, -5.7) * mm});
            skLineSegment(sketch, "E659", {"start": v(49.57, -5.7) * mm, "end": v(49.96, -5.56) * mm});
            skLineSegment(sketch, "E660", {"start": v(49.96, -5.56) * mm, "end": v(50.33, -4.87) * mm});
            skLineSegment(sketch, "E661", {"start": v(50.33, -4.87) * mm, "end": v(50.56, -4.13) * mm});
            skLineSegment(sketch, "E662", {"start": v(50.56, -4.13) * mm, "end": v(50.38, -3.76) * mm});
            skLineSegment(sketch, "E663", {"start": v(50.38, -3.76) * mm, "end": v(49.26, -2.48) * mm});
            skLineSegment(sketch, "E664", {"start": v(49.26, -2.48) * mm, "end": v(48.41, -1.9) * mm});
            skLineSegment(sketch, "E665", {"start": v(48.41, -1.9) * mm, "end": v(48.07, -1.8) * mm});
            skLineSegment(sketch, "E666", {"start": v(48.07, -1.8) * mm, "end": v(46.88, -1.71) * mm});
            skLineSegment(sketch, "E667", {"start": v(46.88, -1.71) * mm, "end": v(46.16, -1.14) * mm});
            skLineSegment(sketch, "E668", {"start": v(46.16, -1.14) * mm, "end": v(46.16, 1.14) * mm});
            skLineSegment(sketch, "E669", {"start": v(46.16, 1.14) * mm, "end": v(46.88, 1.71) * mm});
            skLineSegment(sketch, "E670", {"start": v(46.88, 1.71) * mm, "end": v(48.07, 1.8) * mm});
            skLineSegment(sketch, "E671", {"start": v(48.07, 1.8) * mm, "end": v(48.41, 1.9) * mm});
            skLineSegment(sketch, "E672", {"start": v(48.41, 1.9) * mm, "end": v(49.26, 2.48) * mm});
            skLineSegment(sketch, "E673", {"start": v(49.26, 2.48) * mm, "end": v(50.38, 3.76) * mm});
            skLineSegment(sketch, "E674", {"start": v(50.38, 3.76) * mm, "end": v(50.56, 4.13) * mm});
            skLineSegment(sketch, "E675", {"start": v(50.56, 4.13) * mm, "end": v(50.33, 4.87) * mm});
            skLineSegment(sketch, "E676", {"start": v(50.33, 4.87) * mm, "end": v(49.96, 5.56) * mm});
            skLineSegment(sketch, "E677", {"start": v(49.96, 5.56) * mm, "end": v(49.57, 5.7) * mm});
            skLineSegment(sketch, "E678", {"start": v(49.57, 5.7) * mm, "end": v(47.89, 5.8) * mm});
            skLineSegment(sketch, "E679", {"start": v(47.89, 5.8) * mm, "end": v(46.88, 5.6) * mm});
            skLineSegment(sketch, "E680", {"start": v(46.88, 5.6) * mm, "end": v(46.55, 5.45) * mm});
            skLineSegment(sketch, "E681", {"start": v(46.55, 5.45) * mm, "end": v(45.66, 4.67) * mm});
            skLineSegment(sketch, "E682", {"start": v(45.66, 4.67) * mm, "end": v(44.74, 4.56) * mm});
            skLineSegment(sketch, "E683", {"start": v(44.74, 4.56) * mm, "end": v(43.13, 6.17) * mm});
            skLineSegment(sketch, "E684", {"start": v(43.13, 6.17) * mm, "end": v(43.24, 7.1) * mm});
            skLineSegment(sketch, "E685", {"start": v(43.24, 7.1) * mm, "end": v(44.02, 7.98) * mm});
            skLineSegment(sketch, "E686", {"start": v(44.02, 7.98) * mm, "end": v(44.18, 8.3) * mm});
            skLineSegment(sketch, "E687", {"start": v(44.18, 8.3) * mm, "end": v(44.38, 9.32) * mm});
            skLineSegment(sketch, "E688", {"start": v(44.38, 9.32) * mm, "end": v(44.26, 11) * mm});
            skLineSegment(sketch, "E689", {"start": v(44.26, 11) * mm, "end": v(44.13, 11.4) * mm});
            skLineSegment(sketch, "E690", {"start": v(44.13, 11.4) * mm, "end": v(43.44, 11.76) * mm});
            skLineSegment(sketch, "E691", {"start": v(43.44, 11.76) * mm, "end": v(42.7, 11.99) * mm});
            skLineSegment(sketch, "E692", {"start": v(42.7, 11.99) * mm, "end": v(42.32, 11.8) * mm});
            skLineSegment(sketch, "E693", {"start": v(42.32, 11.8) * mm, "end": v(41.05, 10.7) * mm});
            skLineSegment(sketch, "E694", {"start": v(41.05, 10.7) * mm, "end": v(40.48, 9.84) * mm});
            skLineSegment(sketch, "E695", {"start": v(40.48, 9.84) * mm, "end": v(40.36, 9.5) * mm});
            skLineSegment(sketch, "E696", {"start": v(40.36, 9.5) * mm, "end": v(40.28, 8.32) * mm});
            skLineSegment(sketch, "E697", {"start": v(40.28, 8.32) * mm, "end": v(39.7, 7.59) * mm});
            skLineSegment(sketch, "E698", {"start": v(39.7, 7.59) * mm, "end": v(37.43, 7.59) * mm});
            skLineSegment(sketch, "E699", {"start": v(37.43, 7.59) * mm, "end": v(36.86, 8.32) * mm});
            skLineSegment(sketch, "E700", {"start": v(36.86, 8.32) * mm, "end": v(36.78, 9.5) * mm});
            skLineSegment(sketch, "E701", {"start": v(36.78, 9.5) * mm, "end": v(36.66, 9.84) * mm});
            skLineSegment(sketch, "E702", {"start": v(36.66, 9.84) * mm, "end": v(36.09, 10.7) * mm});
            skLineSegment(sketch, "E703", {"start": v(36.09, 10.7) * mm, "end": v(34.81, 11.8) * mm});
            skLineSegment(sketch, "E704", {"start": v(34.81, 11.8) * mm, "end": v(34.44, 11.99) * mm});
            skLineSegment(sketch, "E705", {"start": v(34.44, 11.99) * mm, "end": v(33.7, 11.76) * mm});
            skLineSegment(sketch, "E706", {"start": v(33.7, 11.76) * mm, "end": v(33, 11.4) * mm});
            skLineSegment(sketch, "E707", {"start": v(33, 11.4) * mm, "end": v(32.88, 11) * mm});
            skLineSegment(sketch, "E708", {"start": v(32.88, 11) * mm, "end": v(32.76, 9.32) * mm});
            skLineSegment(sketch, "E709", {"start": v(32.76, 9.32) * mm, "end": v(32.96, 8.3) * mm});
            skLineSegment(sketch, "E710", {"start": v(32.96, 8.3) * mm, "end": v(33.12, 7.98) * mm});
            skLineSegment(sketch, "E711", {"start": v(33.12, 7.98) * mm, "end": v(33.9, 7.1) * mm});
            skLineSegment(sketch, "E712", {"start": v(33.9, 7.1) * mm, "end": v(34, 6.17) * mm});
            skLineSegment(sketch, "E713", {"start": v(34, 6.17) * mm, "end": v(32.4, 4.56) * mm});
            skLineSegment(sketch, "E714", {"start": v(32.4, 4.56) * mm, "end": v(31.48, 4.67) * mm});
            skLineSegment(sketch, "E715", {"start": v(31.48, 4.67) * mm, "end": v(30.59, 5.45) * mm});
            skLineSegment(sketch, "E716", {"start": v(30.59, 5.45) * mm, "end": v(30.26, 5.6) * mm});
            skLineSegment(sketch, "E717", {"start": v(30.26, 5.6) * mm, "end": v(29.25, 5.8) * mm});
            skLineSegment(sketch, "E718", {"start": v(29.25, 5.8) * mm, "end": v(27.56, 5.7) * mm});
            skLineSegment(sketch, "E719", {"start": v(27.56, 5.7) * mm, "end": v(27.17, 5.56) * mm});
            skLineSegment(sketch, "E720", {"start": v(37.44, 1.65) * mm, "end": v(37.8, 1.85) * mm});
            skLineSegment(sketch, "E721", {"start": v(37.8, 1.85) * mm, "end": v(38.2, 1.97) * mm});
            skLineSegment(sketch, "E722", {"start": v(38.2, 1.97) * mm, "end": v(38.62, 2) * mm});
            skLineSegment(sketch, "E723", {"start": v(38.62, 2) * mm, "end": v(39.04, 1.94) * mm});
            skLineSegment(sketch, "E724", {"start": v(39.04, 1.94) * mm, "end": v(39.43, 1.8) * mm});
            skLineSegment(sketch, "E725", {"start": v(39.43, 1.8) * mm, "end": v(39.79, 1.59) * mm});
            skLineSegment(sketch, "E726", {"start": v(39.79, 1.59) * mm, "end": v(40.09, 1.3) * mm});
            skLineSegment(sketch, "E727", {"start": v(40.09, 1.3) * mm, "end": v(40.33, 0.95) * mm});
            skLineSegment(sketch, "E728", {"start": v(40.33, 0.95) * mm, "end": v(40.49, 0.57) * mm});
            skLineSegment(sketch, "E729", {"start": v(40.49, 0.57) * mm, "end": v(40.56, 0.16) * mm});
            skLineSegment(sketch, "E730", {"start": v(40.56, 0.16) * mm, "end": v(40.55, -0.26) * mm});
            skLineSegment(sketch, "E731", {"start": v(40.55, -0.26) * mm, "end": v(40.45, -0.67) * mm});
            skLineSegment(sketch, "E732", {"start": v(40.45, -0.67) * mm, "end": v(40.27, -1.04) * mm});
            skLineSegment(sketch, "E733", {"start": v(40.27, -1.04) * mm, "end": v(40.02, -1.38) * mm});
            skLineSegment(sketch, "E734", {"start": v(40.02, -1.38) * mm, "end": v(39.7, -1.65) * mm});
            skLineSegment(sketch, "E735", {"start": v(39.7, -1.65) * mm, "end": v(39.33, -1.85) * mm});
            skLineSegment(sketch, "E736", {"start": v(39.33, -1.85) * mm, "end": v(38.93, -1.97) * mm});
            skLineSegment(sketch, "E737", {"start": v(38.93, -1.97) * mm, "end": v(38.52, -2) * mm});
            skLineSegment(sketch, "E738", {"start": v(38.52, -2) * mm, "end": v(38.1, -1.94) * mm});
            skLineSegment(sketch, "E739", {"start": v(38.1, -1.94) * mm, "end": v(37.7, -1.8) * mm});
            skLineSegment(sketch, "E740", {"start": v(37.7, -1.8) * mm, "end": v(37.35, -1.59) * mm});
            skLineSegment(sketch, "E741", {"start": v(37.35, -1.59) * mm, "end": v(37.05, -1.3) * mm});
            skLineSegment(sketch, "E742", {"start": v(37.05, -1.3) * mm, "end": v(36.81, -0.95) * mm});
            skLineSegment(sketch, "E743", {"start": v(36.81, -0.95) * mm, "end": v(36.65, -0.57) * mm});
            skLineSegment(sketch, "E744", {"start": v(36.65, -0.57) * mm, "end": v(36.57, -0.16) * mm});
            skLineSegment(sketch, "E745", {"start": v(36.57, -0.16) * mm, "end": v(36.59, 0.26) * mm});
            skLineSegment(sketch, "E746", {"start": v(36.59, 0.26) * mm, "end": v(36.68, 0.67) * mm});
            skLineSegment(sketch, "E747", {"start": v(36.68, 0.67) * mm, "end": v(36.86, 1.04) * mm});
            skLineSegment(sketch, "E748", {"start": v(36.86, 1.04) * mm, "end": v(37.12, 1.38) * mm});
            skLineSegment(sketch, "E749", {"start": v(37.12, 1.38) * mm, "end": v(37.44, 1.65) * mm});
            skSolve(sketch);
        }
        {
            var Q0;
            Q0=makeQuery(id+"F0.imprint","IMPRINT",FACE,{"disambiguationData":[TD([[makeQuery(id+"F0.imprint","IMPRINT",EDGE,{"derivedFrom":sQuery(id+"F0.wireOp",EDGE,"E0")}),1.0]])]});
            var Q1;
            Q1=makeQuery(id+"F0.imprint","IMPRINT",FACE,{"disambiguationData":[TD([[makeQuery(id+"F0.imprint","IMPRINT",EDGE,{"derivedFrom":sQuery(id+"F0.wireOp",EDGE,"E600")}),1.0]])]});
            extrude(context, id + "F1", {"entities" : qUnion([Q0, Q1]), "depth" : 10 * mm, "offsetDistance" : 25 * mm});
        }
        {
            var Q0;
            Q0=makeQuery(id+"F1.opExtrude","CAP_FACE",FACE,{"disambiguationData":[OSD([sQuery(id+"F0.wireOp",EDGE,"E0"),sQuery(id+"F0.wireOp",EDGE,"E1"),sQuery(id+"F0.wireOp",EDGE,"E2"),sQuery(id+"F0.wireOp",EDGE,"E3"),sQuery(id+"F0.wireOp",EDGE,"E4"),sQuery(id+"F0.wireOp",EDGE,"E5"),sQuery(id+"F0.wireOp",EDGE,"E6"),sQuery(id+"F0.wireOp",EDGE,"E7"),sQuery(id+"F0.wireOp",EDGE,"E8"),sQuery(id+"F0.wireOp",EDGE,"E9"),sQuery(id+"F0.wireOp",EDGE,"E10"),sQuery(id+"F0.wireOp",EDGE,"E11"),sQuery(id+"F0.wireOp",EDGE,"E12"),sQuery(id+"F0.wireOp",EDGE,"E13"),sQuery(id+"F0.wireOp",EDGE,"E14"),sQuery(id+"F0.wireOp",EDGE,"E15"),sQuery(id+"F0.wireOp",EDGE,"E16"),sQuery(id+"F0.wireOp",EDGE,"E17"),sQuery(id+"F0.wireOp",EDGE,"E18"),sQuery(id+"F0.wireOp",EDGE,"E19"),sQuery(id+"F0.wireOp",EDGE,"E20"),sQuery(id+"F0.wireOp",EDGE,"E21"),sQuery(id+"F0.wireOp",EDGE,"E22"),sQuery(id+"F0.wireOp",EDGE,"E23"),sQuery(id+"F0.wireOp",EDGE,"E24"),sQuery(id+"F0.wireOp",EDGE,"E25"),sQuery(id+"F0.wireOp",EDGE,"E26"),sQuery(id+"F0.wireOp",EDGE,"E27"),sQuery(id+"F0.wireOp",EDGE,"E28"),sQuery(id+"F0.wireOp",EDGE,"E29"),sQuery(id+"F0.wireOp",EDGE,"E30"),sQuery(id+"F0.wireOp",EDGE,"E31"),sQuery(id+"F0.wireOp",EDGE,"E32"),sQuery(id+"F0.wireOp",EDGE,"E33"),sQuery(id+"F0.wireOp",EDGE,"E34"),sQuery(id+"F0.wireOp",EDGE,"E35"),sQuery(id+"F0.wireOp",EDGE,"E36"),sQuery(id+"F0.wireOp",EDGE,"E37"),sQuery(id+"F0.wireOp",EDGE,"E38"),sQuery(id+"F0.wireOp",EDGE,"E39"),sQuery(id+"F0.wireOp",EDGE,"E40"),sQuery(id+"F0.wireOp",EDGE,"E41"),sQuery(id+"F0.wireOp",EDGE,"E42"),sQuery(id+"F0.wireOp",EDGE,"E43"),sQuery(id+"F0.wireOp",EDGE,"E44"),sQuery(id+"F0.wireOp",EDGE,"E45"),sQuery(id+"F0.wireOp",EDGE,"E46"),sQuery(id+"F0.wireOp",EDGE,"E47"),sQuery(id+"F0.wireOp",EDGE,"E48"),sQuery(id+"F0.wireOp",EDGE,"E49"),sQuery(id+"F0.wireOp",EDGE,"E50"),sQuery(id+"F0.wireOp",EDGE,"E51"),sQuery(id+"F0.wireOp",EDGE,"E52"),sQuery(id+"F0.wireOp",EDGE,"E53"),sQuery(id+"F0.wireOp",EDGE,"E54"),sQuery(id+"F0.wireOp",EDGE,"E55"),sQuery(id+"F0.wireOp",EDGE,"E56"),sQuery(id+"F0.wireOp",EDGE,"E57"),sQuery(id+"F0.wireOp",EDGE,"E58"),sQuery(id+"F0.wireOp",EDGE,"E59"),sQuery(id+"F0.wireOp",EDGE,"E60"),sQuery(id+"F0.wireOp",EDGE,"E61"),sQuery(id+"F0.wireOp",EDGE,"E62"),sQuery(id+"F0.wireOp",EDGE,"E63"),sQuery(id+"F0.wireOp",EDGE,"E64"),sQuery(id+"F0.wireOp",EDGE,"E65"),sQuery(id+"F0.wireOp",EDGE,"E66"),sQuery(id+"F0.wireOp",EDGE,"E67"),sQuery(id+"F0.wireOp",EDGE,"E68"),sQuery(id+"F0.wireOp",EDGE,"E69"),sQuery(id+"F0.wireOp",EDGE,"E70"),sQuery(id+"F0.wireOp",EDGE,"E71"),sQuery(id+"F0.wireOp",EDGE,"E72"),sQuery(id+"F0.wireOp",EDGE,"E73"),sQuery(id+"F0.wireOp",EDGE,"E74"),sQuery(id+"F0.wireOp",EDGE,"E75"),sQuery(id+"F0.wireOp",EDGE,"E76"),sQuery(id+"F0.wireOp",EDGE,"E77"),sQuery(id+"F0.wireOp",EDGE,"E78"),sQuery(id+"F0.wireOp",EDGE,"E79"),sQuery(id+"F0.wireOp",EDGE,"E80"),sQuery(id+"F0.wireOp",EDGE,"E81"),sQuery(id+"F0.wireOp",EDGE,"E82"),sQuery(id+"F0.wireOp",EDGE,"E83"),sQuery(id+"F0.wireOp",EDGE,"E84"),sQuery(id+"F0.wireOp",EDGE,"E85"),sQuery(id+"F0.wireOp",EDGE,"E86"),sQuery(id+"F0.wireOp",EDGE,"E87"),sQuery(id+"F0.wireOp",EDGE,"E88"),sQuery(id+"F0.wireOp",EDGE,"E89"),sQuery(id+"F0.wireOp",EDGE,"E90"),sQuery(id+"F0.wireOp",EDGE,"E91"),sQuery(id+"F0.wireOp",EDGE,"E92"),sQuery(id+"F0.wireOp",EDGE,"E93"),sQuery(id+"F0.wireOp",EDGE,"E94"),sQuery(id+"F0.wireOp",EDGE,"E95"),sQuery(id+"F0.wireOp",EDGE,"E96"),sQuery(id+"F0.wireOp",EDGE,"E97"),sQuery(id+"F0.wireOp",EDGE,"E98"),sQuery(id+"F0.wireOp",EDGE,"E99"),sQuery(id+"F0.wireOp",EDGE,"E100"),sQuery(id+"F0.wireOp",EDGE,"E101"),sQuery(id+"F0.wireOp",EDGE,"E102"),sQuery(id+"F0.wireOp",EDGE,"E103"),sQuery(id+"F0.wireOp",EDGE,"E104"),sQuery(id+"F0.wireOp",EDGE,"E105"),sQuery(id+"F0.wireOp",EDGE,"E106"),sQuery(id+"F0.wireOp",EDGE,"E107"),sQuery(id+"F0.wireOp",EDGE,"E108"),sQuery(id+"F0.wireOp",EDGE,"E109"),sQuery(id+"F0.wireOp",EDGE,"E110"),sQuery(id+"F0.wireOp",EDGE,"E111"),sQuery(id+"F0.wireOp",EDGE,"E112"),sQuery(id+"F0.wireOp",EDGE,"E113"),sQuery(id+"F0.wireOp",EDGE,"E114"),sQuery(id+"F0.wireOp",EDGE,"E115"),sQuery(id+"F0.wireOp",EDGE,"E116"),sQuery(id+"F0.wireOp",EDGE,"E117"),sQuery(id+"F0.wireOp",EDGE,"E118"),sQuery(id+"F0.wireOp",EDGE,"E119"),sQuery(id+"F0.wireOp",EDGE,"E120"),sQuery(id+"F0.wireOp",EDGE,"E121"),sQuery(id+"F0.wireOp",EDGE,"E122"),sQuery(id+"F0.wireOp",EDGE,"E123"),sQuery(id+"F0.wireOp",EDGE,"E124"),sQuery(id+"F0.wireOp",EDGE,"E125"),sQuery(id+"F0.wireOp",EDGE,"E126"),sQuery(id+"F0.wireOp",EDGE,"E127"),sQuery(id+"F0.wireOp",EDGE,"E128"),sQuery(id+"F0.wireOp",EDGE,"E129"),sQuery(id+"F0.wireOp",EDGE,"E130"),sQuery(id+"F0.wireOp",EDGE,"E131"),sQuery(id+"F0.wireOp",EDGE,"E132"),sQuery(id+"F0.wireOp",EDGE,"E133"),sQuery(id+"F0.wireOp",EDGE,"E134"),sQuery(id+"F0.wireOp",EDGE,"E135"),sQuery(id+"F0.wireOp",EDGE,"E136"),sQuery(id+"F0.wireOp",EDGE,"E137"),sQuery(id+"F0.wireOp",EDGE,"E138"),sQuery(id+"F0.wireOp",EDGE,"E139"),sQuery(id+"F0.wireOp",EDGE,"E140"),sQuery(id+"F0.wireOp",EDGE,"E141"),sQuery(id+"F0.wireOp",EDGE,"E142"),sQuery(id+"F0.wireOp",EDGE,"E143"),sQuery(id+"F0.wireOp",EDGE,"E144"),sQuery(id+"F0.wireOp",EDGE,"E145"),sQuery(id+"F0.wireOp",EDGE,"E146"),sQuery(id+"F0.wireOp",EDGE,"E147"),sQuery(id+"F0.wireOp",EDGE,"E148"),sQuery(id+"F0.wireOp",EDGE,"E149"),sQuery(id+"F0.wireOp",EDGE,"E150"),sQuery(id+"F0.wireOp",EDGE,"E151"),sQuery(id+"F0.wireOp",EDGE,"E152"),sQuery(id+"F0.wireOp",EDGE,"E153"),sQuery(id+"F0.wireOp",EDGE,"E154"),sQuery(id+"F0.wireOp",EDGE,"E155"),sQuery(id+"F0.wireOp",EDGE,"E156"),sQuery(id+"F0.wireOp",EDGE,"E157"),sQuery(id+"F0.wireOp",EDGE,"E158"),sQuery(id+"F0.wireOp",EDGE,"E159"),sQuery(id+"F0.wireOp",EDGE,"E160"),sQuery(id+"F0.wireOp",EDGE,"E161"),sQuery(id+"F0.wireOp",EDGE,"E162"),sQuery(id+"F0.wireOp",EDGE,"E163"),sQuery(id+"F0.wireOp",EDGE,"E164"),sQuery(id+"F0.wireOp",EDGE,"E165"),sQuery(id+"F0.wireOp",EDGE,"E166"),sQuery(id+"F0.wireOp",EDGE,"E167"),sQuery(id+"F0.wireOp",EDGE,"E168"),sQuery(id+"F0.wireOp",EDGE,"E169"),sQuery(id+"F0.wireOp",EDGE,"E170"),sQuery(id+"F0.wireOp",EDGE,"E171"),sQuery(id+"F0.wireOp",EDGE,"E172"),sQuery(id+"F0.wireOp",EDGE,"E173"),sQuery(id+"F0.wireOp",EDGE,"E174"),sQuery(id+"F0.wireOp",EDGE,"E175"),sQuery(id+"F0.wireOp",EDGE,"E176"),sQuery(id+"F0.wireOp",EDGE,"E177"),sQuery(id+"F0.wireOp",EDGE,"E178"),sQuery(id+"F0.wireOp",EDGE,"E179"),sQuery(id+"F0.wireOp",EDGE,"E180"),sQuery(id+"F0.wireOp",EDGE,"E181"),sQuery(id+"F0.wireOp",EDGE,"E182"),sQuery(id+"F0.wireOp",EDGE,"E183"),sQuery(id+"F0.wireOp",EDGE,"E184"),sQuery(id+"F0.wireOp",EDGE,"E185"),sQuery(id+"F0.wireOp",EDGE,"E186"),sQuery(id+"F0.wireOp",EDGE,"E187"),sQuery(id+"F0.wireOp",EDGE,"E188"),sQuery(id+"F0.wireOp",EDGE,"E189"),sQuery(id+"F0.wireOp",EDGE,"E190"),sQuery(id+"F0.wireOp",EDGE,"E191"),sQuery(id+"F0.wireOp",EDGE,"E192"),sQuery(id+"F0.wireOp",EDGE,"E193"),sQuery(id+"F0.wireOp",EDGE,"E194"),sQuery(id+"F0.wireOp",EDGE,"E195"),sQuery(id+"F0.wireOp",EDGE,"E196"),sQuery(id+"F0.wireOp",EDGE,"E197"),sQuery(id+"F0.wireOp",EDGE,"E198"),sQuery(id+"F0.wireOp",EDGE,"E199"),sQuery(id+"F0.wireOp",EDGE,"E200"),sQuery(id+"F0.wireOp",EDGE,"E201"),sQuery(id+"F0.wireOp",EDGE,"E202"),sQuery(id+"F0.wireOp",EDGE,"E203"),sQuery(id+"F0.wireOp",EDGE,"E204"),sQuery(id+"F0.wireOp",EDGE,"E205"),sQuery(id+"F0.wireOp",EDGE,"E206"),sQuery(id+"F0.wireOp",EDGE,"E207"),sQuery(id+"F0.wireOp",EDGE,"E208"),sQuery(id+"F0.wireOp",EDGE,"E209"),sQuery(id+"F0.wireOp",EDGE,"E210"),sQuery(id+"F0.wireOp",EDGE,"E211"),sQuery(id+"F0.wireOp",EDGE,"E212"),sQuery(id+"F0.wireOp",EDGE,"E213"),sQuery(id+"F0.wireOp",EDGE,"E214"),sQuery(id+"F0.wireOp",EDGE,"E215"),sQuery(id+"F0.wireOp",EDGE,"E216"),sQuery(id+"F0.wireOp",EDGE,"E217"),sQuery(id+"F0.wireOp",EDGE,"E218"),sQuery(id+"F0.wireOp",EDGE,"E219"),sQuery(id+"F0.wireOp",EDGE,"E220"),sQuery(id+"F0.wireOp",EDGE,"E221"),sQuery(id+"F0.wireOp",EDGE,"E222"),sQuery(id+"F0.wireOp",EDGE,"E223"),sQuery(id+"F0.wireOp",EDGE,"E224"),sQuery(id+"F0.wireOp",EDGE,"E225"),sQuery(id+"F0.wireOp",EDGE,"E226"),sQuery(id+"F0.wireOp",EDGE,"E227"),sQuery(id+"F0.wireOp",EDGE,"E228"),sQuery(id+"F0.wireOp",EDGE,"E229"),sQuery(id+"F0.wireOp",EDGE,"E230"),sQuery(id+"F0.wireOp",EDGE,"E231"),sQuery(id+"F0.wireOp",EDGE,"E232"),sQuery(id+"F0.wireOp",EDGE,"E233"),sQuery(id+"F0.wireOp",EDGE,"E234"),sQuery(id+"F0.wireOp",EDGE,"E235"),sQuery(id+"F0.wireOp",EDGE,"E236"),sQuery(id+"F0.wireOp",EDGE,"E237"),sQuery(id+"F0.wireOp",EDGE,"E238"),sQuery(id+"F0.wireOp",EDGE,"E239"),sQuery(id+"F0.wireOp",EDGE,"E240"),sQuery(id+"F0.wireOp",EDGE,"E241"),sQuery(id+"F0.wireOp",EDGE,"E242"),sQuery(id+"F0.wireOp",EDGE,"E243"),sQuery(id+"F0.wireOp",EDGE,"E244"),sQuery(id+"F0.wireOp",EDGE,"E245"),sQuery(id+"F0.wireOp",EDGE,"E246"),sQuery(id+"F0.wireOp",EDGE,"E247"),sQuery(id+"F0.wireOp",EDGE,"E248"),sQuery(id+"F0.wireOp",EDGE,"E249"),sQuery(id+"F0.wireOp",EDGE,"E250"),sQuery(id+"F0.wireOp",EDGE,"E251"),sQuery(id+"F0.wireOp",EDGE,"E252"),sQuery(id+"F0.wireOp",EDGE,"E253"),sQuery(id+"F0.wireOp",EDGE,"E254"),sQuery(id+"F0.wireOp",EDGE,"E255"),sQuery(id+"F0.wireOp",EDGE,"E256"),sQuery(id+"F0.wireOp",EDGE,"E257"),sQuery(id+"F0.wireOp",EDGE,"E258"),sQuery(id+"F0.wireOp",EDGE,"E259"),sQuery(id+"F0.wireOp",EDGE,"E260"),sQuery(id+"F0.wireOp",EDGE,"E261"),sQuery(id+"F0.wireOp",EDGE,"E262"),sQuery(id+"F0.wireOp",EDGE,"E263"),sQuery(id+"F0.wireOp",EDGE,"E264"),sQuery(id+"F0.wireOp",EDGE,"E265"),sQuery(id+"F0.wireOp",EDGE,"E266"),sQuery(id+"F0.wireOp",EDGE,"E267"),sQuery(id+"F0.wireOp",EDGE,"E268"),sQuery(id+"F0.wireOp",EDGE,"E269"),sQuery(id+"F0.wireOp",EDGE,"E270"),sQuery(id+"F0.wireOp",EDGE,"E271"),sQuery(id+"F0.wireOp",EDGE,"E272"),sQuery(id+"F0.wireOp",EDGE,"E273"),sQuery(id+"F0.wireOp",EDGE,"E274"),sQuery(id+"F0.wireOp",EDGE,"E275"),sQuery(id+"F0.wireOp",EDGE,"E276"),sQuery(id+"F0.wireOp",EDGE,"E277"),sQuery(id+"F0.wireOp",EDGE,"E278"),sQuery(id+"F0.wireOp",EDGE,"E279"),sQuery(id+"F0.wireOp",EDGE,"E280"),sQuery(id+"F0.wireOp",EDGE,"E281"),sQuery(id+"F0.wireOp",EDGE,"E282"),sQuery(id+"F0.wireOp",EDGE,"E283"),sQuery(id+"F0.wireOp",EDGE,"E284"),sQuery(id+"F0.wireOp",EDGE,"E285"),sQuery(id+"F0.wireOp",EDGE,"E286"),sQuery(id+"F0.wireOp",EDGE,"E287"),sQuery(id+"F0.wireOp",EDGE,"E288"),sQuery(id+"F0.wireOp",EDGE,"E289"),sQuery(id+"F0.wireOp",EDGE,"E290"),sQuery(id+"F0.wireOp",EDGE,"E291"),sQuery(id+"F0.wireOp",EDGE,"E292"),sQuery(id+"F0.wireOp",EDGE,"E293"),sQuery(id+"F0.wireOp",EDGE,"E294"),sQuery(id+"F0.wireOp",EDGE,"E295"),sQuery(id+"F0.wireOp",EDGE,"E296"),sQuery(id+"F0.wireOp",EDGE,"E297"),sQuery(id+"F0.wireOp",EDGE,"E298"),sQuery(id+"F0.wireOp",EDGE,"E299"),sQuery(id+"F0.wireOp",EDGE,"E300"),sQuery(id+"F0.wireOp",EDGE,"E301"),sQuery(id+"F0.wireOp",EDGE,"E302"),sQuery(id+"F0.wireOp",EDGE,"E303"),sQuery(id+"F0.wireOp",EDGE,"E304"),sQuery(id+"F0.wireOp",EDGE,"E305"),sQuery(id+"F0.wireOp",EDGE,"E306"),sQuery(id+"F0.wireOp",EDGE,"E307"),sQuery(id+"F0.wireOp",EDGE,"E308"),sQuery(id+"F0.wireOp",EDGE,"E309"),sQuery(id+"F0.wireOp",EDGE,"E310"),sQuery(id+"F0.wireOp",EDGE,"E311"),sQuery(id+"F0.wireOp",EDGE,"E312"),sQuery(id+"F0.wireOp",EDGE,"E313"),sQuery(id+"F0.wireOp",EDGE,"E314"),sQuery(id+"F0.wireOp",EDGE,"E315"),sQuery(id+"F0.wireOp",EDGE,"E316"),sQuery(id+"F0.wireOp",EDGE,"E317"),sQuery(id+"F0.wireOp",EDGE,"E318"),sQuery(id+"F0.wireOp",EDGE,"E319"),sQuery(id+"F0.wireOp",EDGE,"E320"),sQuery(id+"F0.wireOp",EDGE,"E321"),sQuery(id+"F0.wireOp",EDGE,"E322"),sQuery(id+"F0.wireOp",EDGE,"E323"),sQuery(id+"F0.wireOp",EDGE,"E324"),sQuery(id+"F0.wireOp",EDGE,"E325"),sQuery(id+"F0.wireOp",EDGE,"E326"),sQuery(id+"F0.wireOp",EDGE,"E327"),sQuery(id+"F0.wireOp",EDGE,"E328"),sQuery(id+"F0.wireOp",EDGE,"E329"),sQuery(id+"F0.wireOp",EDGE,"E330"),sQuery(id+"F0.wireOp",EDGE,"E331"),sQuery(id+"F0.wireOp",EDGE,"E332"),sQuery(id+"F0.wireOp",EDGE,"E333"),sQuery(id+"F0.wireOp",EDGE,"E334"),sQuery(id+"F0.wireOp",EDGE,"E335"),sQuery(id+"F0.wireOp",EDGE,"E336"),sQuery(id+"F0.wireOp",EDGE,"E337"),sQuery(id+"F0.wireOp",EDGE,"E338"),sQuery(id+"F0.wireOp",EDGE,"E339"),sQuery(id+"F0.wireOp",EDGE,"E340"),sQuery(id+"F0.wireOp",EDGE,"E341"),sQuery(id+"F0.wireOp",EDGE,"E342"),sQuery(id+"F0.wireOp",EDGE,"E343"),sQuery(id+"F0.wireOp",EDGE,"E344"),sQuery(id+"F0.wireOp",EDGE,"E345"),sQuery(id+"F0.wireOp",EDGE,"E346"),sQuery(id+"F0.wireOp",EDGE,"E347"),sQuery(id+"F0.wireOp",EDGE,"E348"),sQuery(id+"F0.wireOp",EDGE,"E349"),sQuery(id+"F0.wireOp",EDGE,"E350"),sQuery(id+"F0.wireOp",EDGE,"E351"),sQuery(id+"F0.wireOp",EDGE,"E352"),sQuery(id+"F0.wireOp",EDGE,"E353"),sQuery(id+"F0.wireOp",EDGE,"E354"),sQuery(id+"F0.wireOp",EDGE,"E355"),sQuery(id+"F0.wireOp",EDGE,"E356"),sQuery(id+"F0.wireOp",EDGE,"E357"),sQuery(id+"F0.wireOp",EDGE,"E358"),sQuery(id+"F0.wireOp",EDGE,"E359"),sQuery(id+"F0.wireOp",EDGE,"E360"),sQuery(id+"F0.wireOp",EDGE,"E361"),sQuery(id+"F0.wireOp",EDGE,"E362"),sQuery(id+"F0.wireOp",EDGE,"E363"),sQuery(id+"F0.wireOp",EDGE,"E364"),sQuery(id+"F0.wireOp",EDGE,"E365"),sQuery(id+"F0.wireOp",EDGE,"E366"),sQuery(id+"F0.wireOp",EDGE,"E367"),sQuery(id+"F0.wireOp",EDGE,"E368"),sQuery(id+"F0.wireOp",EDGE,"E369"),sQuery(id+"F0.wireOp",EDGE,"E370"),sQuery(id+"F0.wireOp",EDGE,"E371"),sQuery(id+"F0.wireOp",EDGE,"E372"),sQuery(id+"F0.wireOp",EDGE,"E373"),sQuery(id+"F0.wireOp",EDGE,"E374"),sQuery(id+"F0.wireOp",EDGE,"E375"),sQuery(id+"F0.wireOp",EDGE,"E376"),sQuery(id+"F0.wireOp",EDGE,"E377"),sQuery(id+"F0.wireOp",EDGE,"E378"),sQuery(id+"F0.wireOp",EDGE,"E379"),sQuery(id+"F0.wireOp",EDGE,"E380"),sQuery(id+"F0.wireOp",EDGE,"E381"),sQuery(id+"F0.wireOp",EDGE,"E382"),sQuery(id+"F0.wireOp",EDGE,"E383"),sQuery(id+"F0.wireOp",EDGE,"E384"),sQuery(id+"F0.wireOp",EDGE,"E385"),sQuery(id+"F0.wireOp",EDGE,"E386"),sQuery(id+"F0.wireOp",EDGE,"E387"),sQuery(id+"F0.wireOp",EDGE,"E388"),sQuery(id+"F0.wireOp",EDGE,"E389"),sQuery(id+"F0.wireOp",EDGE,"E390"),sQuery(id+"F0.wireOp",EDGE,"E391"),sQuery(id+"F0.wireOp",EDGE,"E392"),sQuery(id+"F0.wireOp",EDGE,"E393"),sQuery(id+"F0.wireOp",EDGE,"E394"),sQuery(id+"F0.wireOp",EDGE,"E395"),sQuery(id+"F0.wireOp",EDGE,"E396"),sQuery(id+"F0.wireOp",EDGE,"E397"),sQuery(id+"F0.wireOp",EDGE,"E398"),sQuery(id+"F0.wireOp",EDGE,"E399"),sQuery(id+"F0.wireOp",EDGE,"E400"),sQuery(id+"F0.wireOp",EDGE,"E401"),sQuery(id+"F0.wireOp",EDGE,"E402"),sQuery(id+"F0.wireOp",EDGE,"E403"),sQuery(id+"F0.wireOp",EDGE,"E404"),sQuery(id+"F0.wireOp",EDGE,"E405"),sQuery(id+"F0.wireOp",EDGE,"E406"),sQuery(id+"F0.wireOp",EDGE,"E407"),sQuery(id+"F0.wireOp",EDGE,"E408"),sQuery(id+"F0.wireOp",EDGE,"E409"),sQuery(id+"F0.wireOp",EDGE,"E410"),sQuery(id+"F0.wireOp",EDGE,"E411"),sQuery(id+"F0.wireOp",EDGE,"E412"),sQuery(id+"F0.wireOp",EDGE,"E413"),sQuery(id+"F0.wireOp",EDGE,"E414"),sQuery(id+"F0.wireOp",EDGE,"E415"),sQuery(id+"F0.wireOp",EDGE,"E416"),sQuery(id+"F0.wireOp",EDGE,"E417"),sQuery(id+"F0.wireOp",EDGE,"E418"),sQuery(id+"F0.wireOp",EDGE,"E419"),sQuery(id+"F0.wireOp",EDGE,"E420"),sQuery(id+"F0.wireOp",EDGE,"E421"),sQuery(id+"F0.wireOp",EDGE,"E422"),sQuery(id+"F0.wireOp",EDGE,"E423"),sQuery(id+"F0.wireOp",EDGE,"E424"),sQuery(id+"F0.wireOp",EDGE,"E425"),sQuery(id+"F0.wireOp",EDGE,"E426"),sQuery(id+"F0.wireOp",EDGE,"E427"),sQuery(id+"F0.wireOp",EDGE,"E428"),sQuery(id+"F0.wireOp",EDGE,"E429"),sQuery(id+"F0.wireOp",EDGE,"E430"),sQuery(id+"F0.wireOp",EDGE,"E431"),sQuery(id+"F0.wireOp",EDGE,"E432"),sQuery(id+"F0.wireOp",EDGE,"E433"),sQuery(id+"F0.wireOp",EDGE,"E434"),sQuery(id+"F0.wireOp",EDGE,"E435"),sQuery(id+"F0.wireOp",EDGE,"E436"),sQuery(id+"F0.wireOp",EDGE,"E437"),sQuery(id+"F0.wireOp",EDGE,"E438"),sQuery(id+"F0.wireOp",EDGE,"E439"),sQuery(id+"F0.wireOp",EDGE,"E440"),sQuery(id+"F0.wireOp",EDGE,"E441"),sQuery(id+"F0.wireOp",EDGE,"E442"),sQuery(id+"F0.wireOp",EDGE,"E443"),sQuery(id+"F0.wireOp",EDGE,"E444"),sQuery(id+"F0.wireOp",EDGE,"E445"),sQuery(id+"F0.wireOp",EDGE,"E446"),sQuery(id+"F0.wireOp",EDGE,"E447"),sQuery(id+"F0.wireOp",EDGE,"E448"),sQuery(id+"F0.wireOp",EDGE,"E449"),sQuery(id+"F0.wireOp",EDGE,"E450"),sQuery(id+"F0.wireOp",EDGE,"E451"),sQuery(id+"F0.wireOp",EDGE,"E452"),sQuery(id+"F0.wireOp",EDGE,"E453"),sQuery(id+"F0.wireOp",EDGE,"E454"),sQuery(id+"F0.wireOp",EDGE,"E455"),sQuery(id+"F0.wireOp",EDGE,"E456"),sQuery(id+"F0.wireOp",EDGE,"E457"),sQuery(id+"F0.wireOp",EDGE,"E458"),sQuery(id+"F0.wireOp",EDGE,"E459"),sQuery(id+"F0.wireOp",EDGE,"E460"),sQuery(id+"F0.wireOp",EDGE,"E461"),sQuery(id+"F0.wireOp",EDGE,"E462"),sQuery(id+"F0.wireOp",EDGE,"E463"),sQuery(id+"F0.wireOp",EDGE,"E464"),sQuery(id+"F0.wireOp",EDGE,"E465"),sQuery(id+"F0.wireOp",EDGE,"E466"),sQuery(id+"F0.wireOp",EDGE,"E467"),sQuery(id+"F0.wireOp",EDGE,"E468"),sQuery(id+"F0.wireOp",EDGE,"E469"),sQuery(id+"F0.wireOp",EDGE,"E470"),sQuery(id+"F0.wireOp",EDGE,"E471"),sQuery(id+"F0.wireOp",EDGE,"E472"),sQuery(id+"F0.wireOp",EDGE,"E473"),sQuery(id+"F0.wireOp",EDGE,"E474"),sQuery(id+"F0.wireOp",EDGE,"E475"),sQuery(id+"F0.wireOp",EDGE,"E476"),sQuery(id+"F0.wireOp",EDGE,"E477"),sQuery(id+"F0.wireOp",EDGE,"E478"),sQuery(id+"F0.wireOp",EDGE,"E479"),sQuery(id+"F0.wireOp",EDGE,"E480"),sQuery(id+"F0.wireOp",EDGE,"E481"),sQuery(id+"F0.wireOp",EDGE,"E482"),sQuery(id+"F0.wireOp",EDGE,"E483"),sQuery(id+"F0.wireOp",EDGE,"E484"),sQuery(id+"F0.wireOp",EDGE,"E485"),sQuery(id+"F0.wireOp",EDGE,"E486"),sQuery(id+"F0.wireOp",EDGE,"E487"),sQuery(id+"F0.wireOp",EDGE,"E488"),sQuery(id+"F0.wireOp",EDGE,"E489"),sQuery(id+"F0.wireOp",EDGE,"E490"),sQuery(id+"F0.wireOp",EDGE,"E491"),sQuery(id+"F0.wireOp",EDGE,"E492"),sQuery(id+"F0.wireOp",EDGE,"E493"),sQuery(id+"F0.wireOp",EDGE,"E494"),sQuery(id+"F0.wireOp",EDGE,"E495"),sQuery(id+"F0.wireOp",EDGE,"E496"),sQuery(id+"F0.wireOp",EDGE,"E497"),sQuery(id+"F0.wireOp",EDGE,"E498"),sQuery(id+"F0.wireOp",EDGE,"E499"),sQuery(id+"F0.wireOp",EDGE,"E500"),sQuery(id+"F0.wireOp",EDGE,"E501"),sQuery(id+"F0.wireOp",EDGE,"E502"),sQuery(id+"F0.wireOp",EDGE,"E503"),sQuery(id+"F0.wireOp",EDGE,"E504"),sQuery(id+"F0.wireOp",EDGE,"E505"),sQuery(id+"F0.wireOp",EDGE,"E506"),sQuery(id+"F0.wireOp",EDGE,"E507"),sQuery(id+"F0.wireOp",EDGE,"E508"),sQuery(id+"F0.wireOp",EDGE,"E509"),sQuery(id+"F0.wireOp",EDGE,"E510"),sQuery(id+"F0.wireOp",EDGE,"E511"),sQuery(id+"F0.wireOp",EDGE,"E512"),sQuery(id+"F0.wireOp",EDGE,"E513"),sQuery(id+"F0.wireOp",EDGE,"E514"),sQuery(id+"F0.wireOp",EDGE,"E515"),sQuery(id+"F0.wireOp",EDGE,"E516"),sQuery(id+"F0.wireOp",EDGE,"E517"),sQuery(id+"F0.wireOp",EDGE,"E518"),sQuery(id+"F0.wireOp",EDGE,"E519"),sQuery(id+"F0.wireOp",EDGE,"E520"),sQuery(id+"F0.wireOp",EDGE,"E521"),sQuery(id+"F0.wireOp",EDGE,"E522"),sQuery(id+"F0.wireOp",EDGE,"E523"),sQuery(id+"F0.wireOp",EDGE,"E524"),sQuery(id+"F0.wireOp",EDGE,"E525"),sQuery(id+"F0.wireOp",EDGE,"E526"),sQuery(id+"F0.wireOp",EDGE,"E527"),sQuery(id+"F0.wireOp",EDGE,"E528"),sQuery(id+"F0.wireOp",EDGE,"E529"),sQuery(id+"F0.wireOp",EDGE,"E530"),sQuery(id+"F0.wireOp",EDGE,"E531"),sQuery(id+"F0.wireOp",EDGE,"E532"),sQuery(id+"F0.wireOp",EDGE,"E533"),sQuery(id+"F0.wireOp",EDGE,"E534"),sQuery(id+"F0.wireOp",EDGE,"E535"),sQuery(id+"F0.wireOp",EDGE,"E536"),sQuery(id+"F0.wireOp",EDGE,"E537"),sQuery(id+"F0.wireOp",EDGE,"E538"),sQuery(id+"F0.wireOp",EDGE,"E539"),sQuery(id+"F0.wireOp",EDGE,"E540"),sQuery(id+"F0.wireOp",EDGE,"E541"),sQuery(id+"F0.wireOp",EDGE,"E542"),sQuery(id+"F0.wireOp",EDGE,"E543"),sQuery(id+"F0.wireOp",EDGE,"E544"),sQuery(id+"F0.wireOp",EDGE,"E545"),sQuery(id+"F0.wireOp",EDGE,"E546"),sQuery(id+"F0.wireOp",EDGE,"E547"),sQuery(id+"F0.wireOp",EDGE,"E548"),sQuery(id+"F0.wireOp",EDGE,"E549"),sQuery(id+"F0.wireOp",EDGE,"E550"),sQuery(id+"F0.wireOp",EDGE,"E551"),sQuery(id+"F0.wireOp",EDGE,"E552"),sQuery(id+"F0.wireOp",EDGE,"E553"),sQuery(id+"F0.wireOp",EDGE,"E554"),sQuery(id+"F0.wireOp",EDGE,"E555"),sQuery(id+"F0.wireOp",EDGE,"E556"),sQuery(id+"F0.wireOp",EDGE,"E557"),sQuery(id+"F0.wireOp",EDGE,"E558"),sQuery(id+"F0.wireOp",EDGE,"E559"),sQuery(id+"F0.wireOp",EDGE,"E560"),sQuery(id+"F0.wireOp",EDGE,"E561"),sQuery(id+"F0.wireOp",EDGE,"E562"),sQuery(id+"F0.wireOp",EDGE,"E563"),sQuery(id+"F0.wireOp",EDGE,"E564"),sQuery(id+"F0.wireOp",EDGE,"E565"),sQuery(id+"F0.wireOp",EDGE,"E566"),sQuery(id+"F0.wireOp",EDGE,"E567"),sQuery(id+"F0.wireOp",EDGE,"E568"),sQuery(id+"F0.wireOp",EDGE,"E569"),sQuery(id+"F0.wireOp",EDGE,"E570"),sQuery(id+"F0.wireOp",EDGE,"E571"),sQuery(id+"F0.wireOp",EDGE,"E572"),sQuery(id+"F0.wireOp",EDGE,"E573"),sQuery(id+"F0.wireOp",EDGE,"E574"),sQuery(id+"F0.wireOp",EDGE,"E575"),sQuery(id+"F0.wireOp",EDGE,"E576"),sQuery(id+"F0.wireOp",EDGE,"E577"),sQuery(id+"F0.wireOp",EDGE,"E578"),sQuery(id+"F0.wireOp",EDGE,"E579"),sQuery(id+"F0.wireOp",EDGE,"E580"),sQuery(id+"F0.wireOp",EDGE,"E581"),sQuery(id+"F0.wireOp",EDGE,"E582"),sQuery(id+"F0.wireOp",EDGE,"E583"),sQuery(id+"F0.wireOp",EDGE,"E584"),sQuery(id+"F0.wireOp",EDGE,"E585"),sQuery(id+"F0.wireOp",EDGE,"E586"),sQuery(id+"F0.wireOp",EDGE,"E587"),sQuery(id+"F0.wireOp",EDGE,"E588"),sQuery(id+"F0.wireOp",EDGE,"E589"),sQuery(id+"F0.wireOp",EDGE,"E590"),sQuery(id+"F0.wireOp",EDGE,"E591"),sQuery(id+"F0.wireOp",EDGE,"E592"),sQuery(id+"F0.wireOp",EDGE,"E593"),sQuery(id+"F0.wireOp",EDGE,"E594"),sQuery(id+"F0.wireOp",EDGE,"E595"),sQuery(id+"F0.wireOp",EDGE,"E596"),sQuery(id+"F0.wireOp",EDGE,"E597"),sQuery(id+"F0.wireOp",EDGE,"E598"),sQuery(id+"F0.wireOp",EDGE,"E599")])],"isStart":true});
            var sketch = newSketch(context, id + "F2", { "sketchPlane" : qUnion([Q0])});
            skLineSegment(sketch, "E750", {"start": v(8, 0.8) * mm, "end": v(10.32, -0.23) * mm, "construction": true});
            skLineSegment(sketch, "E751", {"start": v(8.2, 1.17) * mm, "end": v(10.5, -0.5) * mm, "construction": true});
            skLineSegment(sketch, "E752", {"start": v(9.6, -1.98) * mm, "end": v(9.84, 0.27) * mm, "construction": true});
            skCircle(sketch, "E753", {"center": v(9.81, 0) * mm, "radius": 3.18 * mm});
            skSolve(sketch);
        }
        {
            var Q0;
            Q0=makeQuery(id+"F2.imprint","IMPRINT",FACE,{"disambiguationData":[TD([[makeQuery(id+"F2.imprint","IMPRINT",EDGE,{"derivedFrom":sQuery(id+"F2.wireOp",EDGE,"E753")}),1.0]])]});
            extrude(context, id + "F3", {"entities" : qUnion([Q0]), "operationType" : NewBodyOperationType.REMOVE, "oppositeDirection" : true, "depth" : 36.7 * mm, "offsetDistance" : 25 * mm});
        }
        {
            var Q0;
            Q0=makeQuery(id+"F1.opExtrude","CAP_FACE",FACE,{"disambiguationData":[OSD([sQuery(id+"F0.wireOp",EDGE,"E600"),sQuery(id+"F0.wireOp",EDGE,"E601"),sQuery(id+"F0.wireOp",EDGE,"E602"),sQuery(id+"F0.wireOp",EDGE,"E603"),sQuery(id+"F0.wireOp",EDGE,"E604"),sQuery(id+"F0.wireOp",EDGE,"E605"),sQuery(id+"F0.wireOp",EDGE,"E606"),sQuery(id+"F0.wireOp",EDGE,"E607"),sQuery(id+"F0.wireOp",EDGE,"E608"),sQuery(id+"F0.wireOp",EDGE,"E609"),sQuery(id+"F0.wireOp",EDGE,"E610"),sQuery(id+"F0.wireOp",EDGE,"E611"),sQuery(id+"F0.wireOp",EDGE,"E612"),sQuery(id+"F0.wireOp",EDGE,"E613"),sQuery(id+"F0.wireOp",EDGE,"E614"),sQuery(id+"F0.wireOp",EDGE,"E615"),sQuery(id+"F0.wireOp",EDGE,"E616"),sQuery(id+"F0.wireOp",EDGE,"E617"),sQuery(id+"F0.wireOp",EDGE,"E618"),sQuery(id+"F0.wireOp",EDGE,"E619"),sQuery(id+"F0.wireOp",EDGE,"E620"),sQuery(id+"F0.wireOp",EDGE,"E621"),sQuery(id+"F0.wireOp",EDGE,"E622"),sQuery(id+"F0.wireOp",EDGE,"E623"),sQuery(id+"F0.wireOp",EDGE,"E624"),sQuery(id+"F0.wireOp",EDGE,"E625"),sQuery(id+"F0.wireOp",EDGE,"E626"),sQuery(id+"F0.wireOp",EDGE,"E627"),sQuery(id+"F0.wireOp",EDGE,"E628"),sQuery(id+"F0.wireOp",EDGE,"E629"),sQuery(id+"F0.wireOp",EDGE,"E630"),sQuery(id+"F0.wireOp",EDGE,"E631"),sQuery(id+"F0.wireOp",EDGE,"E632"),sQuery(id+"F0.wireOp",EDGE,"E633"),sQuery(id+"F0.wireOp",EDGE,"E634"),sQuery(id+"F0.wireOp",EDGE,"E635"),sQuery(id+"F0.wireOp",EDGE,"E636"),sQuery(id+"F0.wireOp",EDGE,"E637"),sQuery(id+"F0.wireOp",EDGE,"E638"),sQuery(id+"F0.wireOp",EDGE,"E639"),sQuery(id+"F0.wireOp",EDGE,"E640"),sQuery(id+"F0.wireOp",EDGE,"E641"),sQuery(id+"F0.wireOp",EDGE,"E642"),sQuery(id+"F0.wireOp",EDGE,"E643"),sQuery(id+"F0.wireOp",EDGE,"E644"),sQuery(id+"F0.wireOp",EDGE,"E645"),sQuery(id+"F0.wireOp",EDGE,"E646"),sQuery(id+"F0.wireOp",EDGE,"E647"),sQuery(id+"F0.wireOp",EDGE,"E648"),sQuery(id+"F0.wireOp",EDGE,"E649"),sQuery(id+"F0.wireOp",EDGE,"E650"),sQuery(id+"F0.wireOp",EDGE,"E651"),sQuery(id+"F0.wireOp",EDGE,"E652"),sQuery(id+"F0.wireOp",EDGE,"E653"),sQuery(id+"F0.wireOp",EDGE,"E654"),sQuery(id+"F0.wireOp",EDGE,"E655"),sQuery(id+"F0.wireOp",EDGE,"E656"),sQuery(id+"F0.wireOp",EDGE,"E657"),sQuery(id+"F0.wireOp",EDGE,"E658"),sQuery(id+"F0.wireOp",EDGE,"E659"),sQuery(id+"F0.wireOp",EDGE,"E660"),sQuery(id+"F0.wireOp",EDGE,"E661"),sQuery(id+"F0.wireOp",EDGE,"E662"),sQuery(id+"F0.wireOp",EDGE,"E663"),sQuery(id+"F0.wireOp",EDGE,"E664"),sQuery(id+"F0.wireOp",EDGE,"E665"),sQuery(id+"F0.wireOp",EDGE,"E666"),sQuery(id+"F0.wireOp",EDGE,"E667"),sQuery(id+"F0.wireOp",EDGE,"E668"),sQuery(id+"F0.wireOp",EDGE,"E669"),sQuery(id+"F0.wireOp",EDGE,"E670"),sQuery(id+"F0.wireOp",EDGE,"E671"),sQuery(id+"F0.wireOp",EDGE,"E672"),sQuery(id+"F0.wireOp",EDGE,"E673"),sQuery(id+"F0.wireOp",EDGE,"E674"),sQuery(id+"F0.wireOp",EDGE,"E675"),sQuery(id+"F0.wireOp",EDGE,"E676"),sQuery(id+"F0.wireOp",EDGE,"E677"),sQuery(id+"F0.wireOp",EDGE,"E678"),sQuery(id+"F0.wireOp",EDGE,"E679"),sQuery(id+"F0.wireOp",EDGE,"E680"),sQuery(id+"F0.wireOp",EDGE,"E681"),sQuery(id+"F0.wireOp",EDGE,"E682"),sQuery(id+"F0.wireOp",EDGE,"E683"),sQuery(id+"F0.wireOp",EDGE,"E684"),sQuery(id+"F0.wireOp",EDGE,"E685"),sQuery(id+"F0.wireOp",EDGE,"E686"),sQuery(id+"F0.wireOp",EDGE,"E687"),sQuery(id+"F0.wireOp",EDGE,"E688"),sQuery(id+"F0.wireOp",EDGE,"E689"),sQuery(id+"F0.wireOp",EDGE,"E690"),sQuery(id+"F0.wireOp",EDGE,"E691"),sQuery(id+"F0.wireOp",EDGE,"E692"),sQuery(id+"F0.wireOp",EDGE,"E693"),sQuery(id+"F0.wireOp",EDGE,"E694"),sQuery(id+"F0.wireOp",EDGE,"E695"),sQuery(id+"F0.wireOp",EDGE,"E696"),sQuery(id+"F0.wireOp",EDGE,"E697"),sQuery(id+"F0.wireOp",EDGE,"E698"),sQuery(id+"F0.wireOp",EDGE,"E699"),sQuery(id+"F0.wireOp",EDGE,"E700"),sQuery(id+"F0.wireOp",EDGE,"E701"),sQuery(id+"F0.wireOp",EDGE,"E702"),sQuery(id+"F0.wireOp",EDGE,"E703"),sQuery(id+"F0.wireOp",EDGE,"E704"),sQuery(id+"F0.wireOp",EDGE,"E705"),sQuery(id+"F0.wireOp",EDGE,"E706"),sQuery(id+"F0.wireOp",EDGE,"E707"),sQuery(id+"F0.wireOp",EDGE,"E708"),sQuery(id+"F0.wireOp",EDGE,"E709"),sQuery(id+"F0.wireOp",EDGE,"E710"),sQuery(id+"F0.wireOp",EDGE,"E711"),sQuery(id+"F0.wireOp",EDGE,"E712"),sQuery(id+"F0.wireOp",EDGE,"E713"),sQuery(id+"F0.wireOp",EDGE,"E714"),sQuery(id+"F0.wireOp",EDGE,"E715"),sQuery(id+"F0.wireOp",EDGE,"E716"),sQuery(id+"F0.wireOp",EDGE,"E717"),sQuery(id+"F0.wireOp",EDGE,"E718"),sQuery(id+"F0.wireOp",EDGE,"E719"),sQuery(id+"F0.wireOp",EDGE,"E720"),sQuery(id+"F0.wireOp",EDGE,"E721"),sQuery(id+"F0.wireOp",EDGE,"E722"),sQuery(id+"F0.wireOp",EDGE,"E723"),sQuery(id+"F0.wireOp",EDGE,"E724"),sQuery(id+"F0.wireOp",EDGE,"E725"),sQuery(id+"F0.wireOp",EDGE,"E726"),sQuery(id+"F0.wireOp",EDGE,"E727"),sQuery(id+"F0.wireOp",EDGE,"E728"),sQuery(id+"F0.wireOp",EDGE,"E729"),sQuery(id+"F0.wireOp",EDGE,"E730"),sQuery(id+"F0.wireOp",EDGE,"E731"),sQuery(id+"F0.wireOp",EDGE,"E732"),sQuery(id+"F0.wireOp",EDGE,"E733"),sQuery(id+"F0.wireOp",EDGE,"E734"),sQuery(id+"F0.wireOp",EDGE,"E735"),sQuery(id+"F0.wireOp",EDGE,"E736"),sQuery(id+"F0.wireOp",EDGE,"E737"),sQuery(id+"F0.wireOp",EDGE,"E738"),sQuery(id+"F0.wireOp",EDGE,"E739"),sQuery(id+"F0.wireOp",EDGE,"E740"),sQuery(id+"F0.wireOp",EDGE,"E741"),sQuery(id+"F0.wireOp",EDGE,"E742"),sQuery(id+"F0.wireOp",EDGE,"E743"),sQuery(id+"F0.wireOp",EDGE,"E744"),sQuery(id+"F0.wireOp",EDGE,"E745"),sQuery(id+"F0.wireOp",EDGE,"E746"),sQuery(id+"F0.wireOp",EDGE,"E747"),sQuery(id+"F0.wireOp",EDGE,"E748"),sQuery(id+"F0.wireOp",EDGE,"E749")])],"isStart":true});
            var sketch = newSketch(context, id + "F4", { "sketchPlane" : qUnion([Q0])});
            skLineSegment(sketch, "E754", {"start": v(-37, 1.21) * mm, "end": v(-39.83, -0.97) * mm, "construction": true});
            skLineSegment(sketch, "E755", {"start": v(-36.63, 0.46) * mm, "end": v(-38.91, -0.08) * mm, "construction": true});
            skCircle(sketch, "E756", {"center": v(-38.57, 0) * mm, "radius": 2.5 * mm});
            skSolve(sketch);
        }
        {
            var Q0;
            Q0=makeQuery(id+"F4.imprint","IMPRINT",FACE,{"disambiguationData":[TD([[makeQuery(id+"F4.imprint","IMPRINT",EDGE,{"derivedFrom":sQuery(id+"F4.wireOp",EDGE,"E756")}),1.0]])]});
            extrude(context, id + "F5", {"entities" : qUnion([Q0]), "operationType" : NewBodyOperationType.REMOVE, "oppositeDirection" : true, "depth" : 56 * mm, "offsetDistance" : 25 * mm});
        }
        {
            var Q0;
            Q0=makeQuery(id+"F1.opExtrude","CAP_FACE",FACE,{"disambiguationData":[OSD([sQuery(id+"F0.wireOp",EDGE,"E600"),sQuery(id+"F0.wireOp",EDGE,"E601"),sQuery(id+"F0.wireOp",EDGE,"E602"),sQuery(id+"F0.wireOp",EDGE,"E603"),sQuery(id+"F0.wireOp",EDGE,"E604"),sQuery(id+"F0.wireOp",EDGE,"E605"),sQuery(id+"F0.wireOp",EDGE,"E606"),sQuery(id+"F0.wireOp",EDGE,"E607"),sQuery(id+"F0.wireOp",EDGE,"E608"),sQuery(id+"F0.wireOp",EDGE,"E609"),sQuery(id+"F0.wireOp",EDGE,"E610"),sQuery(id+"F0.wireOp",EDGE,"E611"),sQuery(id+"F0.wireOp",EDGE,"E612"),sQuery(id+"F0.wireOp",EDGE,"E613"),sQuery(id+"F0.wireOp",EDGE,"E614"),sQuery(id+"F0.wireOp",EDGE,"E615"),sQuery(id+"F0.wireOp",EDGE,"E616"),sQuery(id+"F0.wireOp",EDGE,"E617"),sQuery(id+"F0.wireOp",EDGE,"E618"),sQuery(id+"F0.wireOp",EDGE,"E619"),sQuery(id+"F0.wireOp",EDGE,"E620"),sQuery(id+"F0.wireOp",EDGE,"E621"),sQuery(id+"F0.wireOp",EDGE,"E622"),sQuery(id+"F0.wireOp",EDGE,"E623"),sQuery(id+"F0.wireOp",EDGE,"E624"),sQuery(id+"F0.wireOp",EDGE,"E625"),sQuery(id+"F0.wireOp",EDGE,"E626"),sQuery(id+"F0.wireOp",EDGE,"E627"),sQuery(id+"F0.wireOp",EDGE,"E628"),sQuery(id+"F0.wireOp",EDGE,"E629"),sQuery(id+"F0.wireOp",EDGE,"E630"),sQuery(id+"F0.wireOp",EDGE,"E631"),sQuery(id+"F0.wireOp",EDGE,"E632"),sQuery(id+"F0.wireOp",EDGE,"E633"),sQuery(id+"F0.wireOp",EDGE,"E634"),sQuery(id+"F0.wireOp",EDGE,"E635"),sQuery(id+"F0.wireOp",EDGE,"E636"),sQuery(id+"F0.wireOp",EDGE,"E637"),sQuery(id+"F0.wireOp",EDGE,"E638"),sQuery(id+"F0.wireOp",EDGE,"E639"),sQuery(id+"F0.wireOp",EDGE,"E640"),sQuery(id+"F0.wireOp",EDGE,"E641"),sQuery(id+"F0.wireOp",EDGE,"E642"),sQuery(id+"F0.wireOp",EDGE,"E643"),sQuery(id+"F0.wireOp",EDGE,"E644"),sQuery(id+"F0.wireOp",EDGE,"E645"),sQuery(id+"F0.wireOp",EDGE,"E646"),sQuery(id+"F0.wireOp",EDGE,"E647"),sQuery(id+"F0.wireOp",EDGE,"E648"),sQuery(id+"F0.wireOp",EDGE,"E649"),sQuery(id+"F0.wireOp",EDGE,"E650"),sQuery(id+"F0.wireOp",EDGE,"E651"),sQuery(id+"F0.wireOp",EDGE,"E652"),sQuery(id+"F0.wireOp",EDGE,"E653"),sQuery(id+"F0.wireOp",EDGE,"E654"),sQuery(id+"F0.wireOp",EDGE,"E655"),sQuery(id+"F0.wireOp",EDGE,"E656"),sQuery(id+"F0.wireOp",EDGE,"E657"),sQuery(id+"F0.wireOp",EDGE,"E658"),sQuery(id+"F0.wireOp",EDGE,"E659"),sQuery(id+"F0.wireOp",EDGE,"E660"),sQuery(id+"F0.wireOp",EDGE,"E661"),sQuery(id+"F0.wireOp",EDGE,"E662"),sQuery(id+"F0.wireOp",EDGE,"E663"),sQuery(id+"F0.wireOp",EDGE,"E664"),sQuery(id+"F0.wireOp",EDGE,"E665"),sQuery(id+"F0.wireOp",EDGE,"E666"),sQuery(id+"F0.wireOp",EDGE,"E667"),sQuery(id+"F0.wireOp",EDGE,"E668"),sQuery(id+"F0.wireOp",EDGE,"E669"),sQuery(id+"F0.wireOp",EDGE,"E670"),sQuery(id+"F0.wireOp",EDGE,"E671"),sQuery(id+"F0.wireOp",EDGE,"E672"),sQuery(id+"F0.wireOp",EDGE,"E673"),sQuery(id+"F0.wireOp",EDGE,"E674"),sQuery(id+"F0.wireOp",EDGE,"E675"),sQuery(id+"F0.wireOp",EDGE,"E676"),sQuery(id+"F0.wireOp",EDGE,"E677"),sQuery(id+"F0.wireOp",EDGE,"E678"),sQuery(id+"F0.wireOp",EDGE,"E679"),sQuery(id+"F0.wireOp",EDGE,"E680"),sQuery(id+"F0.wireOp",EDGE,"E681"),sQuery(id+"F0.wireOp",EDGE,"E682"),sQuery(id+"F0.wireOp",EDGE,"E683"),sQuery(id+"F0.wireOp",EDGE,"E684"),sQuery(id+"F0.wireOp",EDGE,"E685"),sQuery(id+"F0.wireOp",EDGE,"E686"),sQuery(id+"F0.wireOp",EDGE,"E687"),sQuery(id+"F0.wireOp",EDGE,"E688"),sQuery(id+"F0.wireOp",EDGE,"E689"),sQuery(id+"F0.wireOp",EDGE,"E690"),sQuery(id+"F0.wireOp",EDGE,"E691"),sQuery(id+"F0.wireOp",EDGE,"E692"),sQuery(id+"F0.wireOp",EDGE,"E693"),sQuery(id+"F0.wireOp",EDGE,"E694"),sQuery(id+"F0.wireOp",EDGE,"E695"),sQuery(id+"F0.wireOp",EDGE,"E696"),sQuery(id+"F0.wireOp",EDGE,"E697"),sQuery(id+"F0.wireOp",EDGE,"E698"),sQuery(id+"F0.wireOp",EDGE,"E699"),sQuery(id+"F0.wireOp",EDGE,"E700"),sQuery(id+"F0.wireOp",EDGE,"E701"),sQuery(id+"F0.wireOp",EDGE,"E702"),sQuery(id+"F0.wireOp",EDGE,"E703"),sQuery(id+"F0.wireOp",EDGE,"E704"),sQuery(id+"F0.wireOp",EDGE,"E705"),sQuery(id+"F0.wireOp",EDGE,"E706"),sQuery(id+"F0.wireOp",EDGE,"E707"),sQuery(id+"F0.wireOp",EDGE,"E708"),sQuery(id+"F0.wireOp",EDGE,"E709"),sQuery(id+"F0.wireOp",EDGE,"E710"),sQuery(id+"F0.wireOp",EDGE,"E711"),sQuery(id+"F0.wireOp",EDGE,"E712"),sQuery(id+"F0.wireOp",EDGE,"E713"),sQuery(id+"F0.wireOp",EDGE,"E714"),sQuery(id+"F0.wireOp",EDGE,"E715"),sQuery(id+"F0.wireOp",EDGE,"E716"),sQuery(id+"F0.wireOp",EDGE,"E717"),sQuery(id+"F0.wireOp",EDGE,"E718"),sQuery(id+"F0.wireOp",EDGE,"E719"),sQuery(id+"F0.wireOp",EDGE,"E720"),sQuery(id+"F0.wireOp",EDGE,"E721"),sQuery(id+"F0.wireOp",EDGE,"E722"),sQuery(id+"F0.wireOp",EDGE,"E723"),sQuery(id+"F0.wireOp",EDGE,"E724"),sQuery(id+"F0.wireOp",EDGE,"E725"),sQuery(id+"F0.wireOp",EDGE,"E726"),sQuery(id+"F0.wireOp",EDGE,"E727"),sQuery(id+"F0.wireOp",EDGE,"E728"),sQuery(id+"F0.wireOp",EDGE,"E729"),sQuery(id+"F0.wireOp",EDGE,"E730"),sQuery(id+"F0.wireOp",EDGE,"E731"),sQuery(id+"F0.wireOp",EDGE,"E732"),sQuery(id+"F0.wireOp",EDGE,"E733"),sQuery(id+"F0.wireOp",EDGE,"E734"),sQuery(id+"F0.wireOp",EDGE,"E735"),sQuery(id+"F0.wireOp",EDGE,"E736"),sQuery(id+"F0.wireOp",EDGE,"E737"),sQuery(id+"F0.wireOp",EDGE,"E738"),sQuery(id+"F0.wireOp",EDGE,"E739"),sQuery(id+"F0.wireOp",EDGE,"E740"),sQuery(id+"F0.wireOp",EDGE,"E741"),sQuery(id+"F0.wireOp",EDGE,"E742"),sQuery(id+"F0.wireOp",EDGE,"E743"),sQuery(id+"F0.wireOp",EDGE,"E744"),sQuery(id+"F0.wireOp",EDGE,"E745"),sQuery(id+"F0.wireOp",EDGE,"E746"),sQuery(id+"F0.wireOp",EDGE,"E747"),sQuery(id+"F0.wireOp",EDGE,"E748"),sQuery(id+"F0.wireOp",EDGE,"E749")])],"isStart":false});
            extrude(context, id + "F6", {"entities" : qUnion([Q0]), "operationType" : NewBodyOperationType.ADD, "depth" : 2 * mm, "offsetDistance" : 25 * mm});
        }
    });
